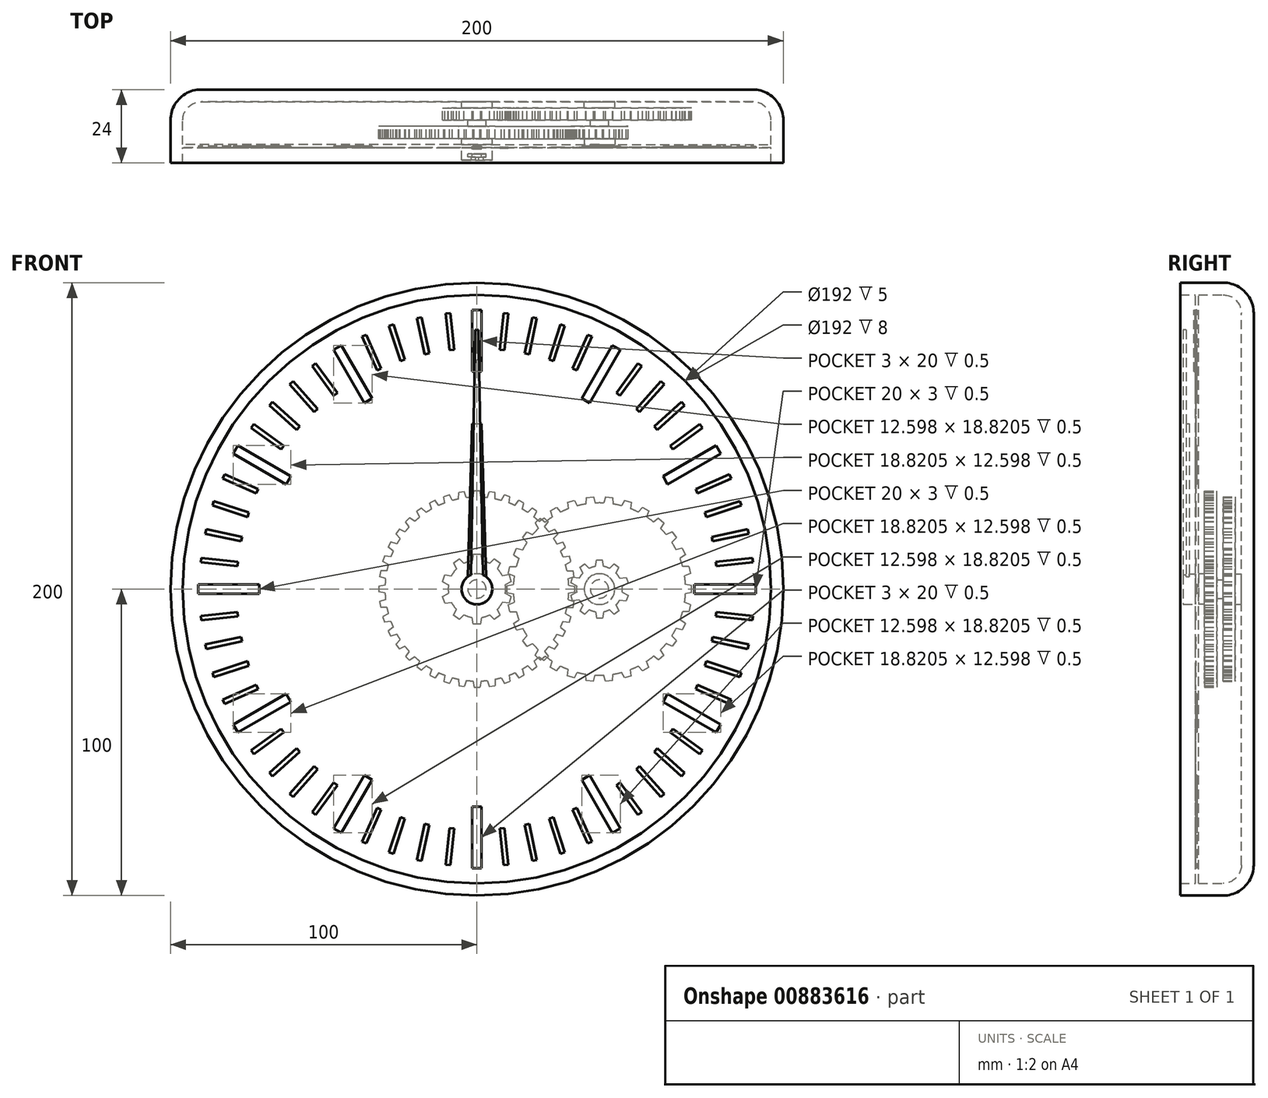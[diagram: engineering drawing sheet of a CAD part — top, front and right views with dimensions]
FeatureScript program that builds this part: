
annotation { "Feature Type Name" : "Feature", "Feature Type Description" : "" }
export const myFeature = defineFeature(function(context is Context, id is Id, definition is map)
    precondition{}
    {
        {
            var Q0;
            Q0=qCreatedBy(makeId("Front.planeOp"),FACE);
            var sketch = newSketch(context, id + "F0", { "sketchPlane" : qUnion([Q0])});
            skCircle(sketch, "E0", {"center": v(0, 0) * mm, "radius": 100 * mm});
            skSolve(sketch);
        }
        {
            var Q0;
            Q0 = qSketchRegion(id + "F0", true);
            extrude(context, id + "F1", {"entities" : qUnion([Q0]), "depth" : 24 * mm, "offsetDistance" : 25 * mm});
        }
        {
            var Q0;
            Q0=makeQuery(id+"F1.opExtrude","CAP_EDGE",EDGE,{"disambiguationData":[OSD([sQuery(id+"F0.wireOp",EDGE,"E0")])],"isStart":true});
            fillet(context, id + "F2", {"entities" : qUnion([Q0]), "radius" : 10 * mm, "tangentPropagation" : true, "allowEdgeOverflow" : false});
        }
        {
            var Q0;
            Q0=makeQuery(id+"F1.opExtrude","CAP_FACE",FACE,{"disambiguationData":[OSD([sQuery(id+"F0.wireOp",EDGE,"E0")])],"isStart":false});
            shell(context, id + "F3", {"entities" : qUnion([Q0]), "thickness" : 4 * mm});
        }
        {
            var Q0;
            {var subQ0=sQuery(id+"F0.wireOp",EDGE,"E0");Q0=makeQuery(id+"F3.opShell","OFFSET_FACE",FACE,{"disambiguationData":[OSD([subQ0]),TDD([makeQuery(id+"F1.opExtrude","CAP_FACE",FACE,{"disambiguationData":[OSD([subQ0])],"isStart":true})])]});}
            var sketch = newSketch(context, id + "F4", { "sketchPlane" : qUnion([Q0])});
            skCircle(sketch, "E1", {"center": v(0, 0) * mm, "radius": 3 * mm});
            skCircle(sketch, "E2", {"center": v(0, 0) * mm, "radius": 5 * mm});
            skCircle(sketch, "E3", {"center": v(40, 0) * mm, "radius": 3 * mm});
            skCircle(sketch, "E4", {"center": v(40, 0) * mm, "radius": 5 * mm});
            skSolve(sketch);
        }
        {
            var Q0;
            Q0 = qSketchRegion(id + "F4", true);
            extrude(context, id + "F5", {"entities" : qUnion([Q0]), "operationType" : NewBodyOperationType.ADD, "depth" : 2 * mm, "offsetDistance" : 25 * mm});
        }
        {
            var Q0;
            {var subQ0=sQuery(id+"F0.wireOp",EDGE,"E0");Q0=makeQuery(id+"F5.boolean.opBoolean","SPLIT",FACE,{"disambiguationData":[TD([makeQuery(id+"F5.opExtrude","SWEPT_FACE",FACE,{"disambiguationData":[OSD([sQuery(id+"F4.wireOp",EDGE,"E1")])]})])],"derivedFrom":makeQuery(id+"F3.opShell","OFFSET_FACE",FACE,{"disambiguationData":[OSD([subQ0]),TDD([makeQuery(id+"F1.opExtrude","CAP_FACE",FACE,{"disambiguationData":[OSD([subQ0])],"isStart":true})])]})});}
            extrude(context, id + "F6", {"entities" : qUnion([Q0]), "depth" : 19 * mm, "offsetDistance" : 25 * mm});
        }
        {
            var Q0;
            {var subQ0=sQuery(id+"F0.wireOp",EDGE,"E0");Q0=makeQuery(id+"F5.boolean.opBoolean","SPLIT",FACE,{"disambiguationData":[TD([makeQuery(id+"F5.opExtrude","SWEPT_FACE",FACE,{"disambiguationData":[OSD([sQuery(id+"F4.wireOp",EDGE,"E3")])]})])],"derivedFrom":makeQuery(id+"F3.opShell","OFFSET_FACE",FACE,{"disambiguationData":[OSD([subQ0]),TDD([makeQuery(id+"F1.opExtrude","CAP_FACE",FACE,{"disambiguationData":[OSD([subQ0])],"isStart":true})])]})});}
            extrude(context, id + "F7", {"entities" : qUnion([Q0]), "depth" : 8 * mm, "offsetDistance" : 25 * mm});
        }
        {
            var Q0;
            Q0=makeQuery(id+"F5.opExtrude","CAP_FACE",FACE,{"disambiguationData":[OSD([sQuery(id+"F4.wireOp",EDGE,"E1"),sQuery(id+"F4.wireOp",EDGE,"E2")])],"isStart":false});
            var sketch = newSketch(context, id + "F8", { "sketchPlane" : qUnion([Q0])});
            skCircle(sketch, "E5", {"center": v(0, 0) * mm, "radius": 9.38 * mm});
            skLineSegment(sketch, "E6", {"start": v(0, 11.38) * mm, "end": v(1.18, 11.38) * mm});
            skLineSegment(sketch, "E7", {"start": v(1.18, 11.38) * mm, "end": v(1.55, 9.25) * mm});
            skLineSegment(sketch, "E8.MirrorCS", {"start": v(0, 11.38) * mm, "end": v(-1.18, 11.38) * mm});
            skLineSegment(sketch, "E9.MirrorCS", {"start": v(-1.18, 11.38) * mm, "end": v(-1.55, 9.25) * mm});
            skLineSegment(sketch, "E10.1.0", {"start": v(-6.69, 9.2) * mm, "end": v(-7.64, 8.51) * mm});
            skLineSegment(sketch, "E10.1.1", {"start": v(-6.69, 9.2) * mm, "end": v(-5.73, 9.9) * mm});
            skLineSegment(sketch, "E10.1.2", {"start": v(-5.73, 9.9) * mm, "end": v(-4.18, 8.4) * mm});
            skLineSegment(sketch, "E10.1.3", {"start": v(-7.64, 8.51) * mm, "end": v(-6.7, 6.57) * mm});
            skLineSegment(sketch, "E10.2.0", {"start": v(-10.82, 3.52) * mm, "end": v(-11.18, 2.4) * mm});
            skLineSegment(sketch, "E10.2.1", {"start": v(-10.82, 3.52) * mm, "end": v(-10.45, 4.64) * mm});
            skLineSegment(sketch, "E10.2.2", {"start": v(-10.45, 4.64) * mm, "end": v(-8.31, 4.33) * mm});
            skLineSegment(sketch, "E10.2.3", {"start": v(-11.18, 2.4) * mm, "end": v(-9.27, 1.38) * mm});
            skLineSegment(sketch, "E11.2.3.0", {"start": v(-10.82, -3.52) * mm, "end": v(-10.45, -4.64) * mm});
            skLineSegment(sketch, "E11.3.3.0", {"start": v(-10.82, -3.52) * mm, "end": v(-11.18, -2.4) * mm});
            skLineSegment(sketch, "E11.6.3.0", {"start": v(-11.18, -2.4) * mm, "end": v(-9.27, -1.38) * mm});
            skLineSegment(sketch, "E11.9.3.0", {"start": v(-10.45, -4.64) * mm, "end": v(-8.31, -4.33) * mm});
            skLineSegment(sketch, "E11.2.4.0", {"start": v(-6.69, -9.2) * mm, "end": v(-5.73, -9.9) * mm});
            skLineSegment(sketch, "E11.3.4.0", {"start": v(-6.69, -9.2) * mm, "end": v(-7.64, -8.51) * mm});
            skLineSegment(sketch, "E11.6.4.0", {"start": v(-7.64, -8.51) * mm, "end": v(-6.7, -6.57) * mm});
            skLineSegment(sketch, "E11.9.4.0", {"start": v(-5.73, -9.9) * mm, "end": v(-4.18, -8.4) * mm});
            skLineSegment(sketch, "E11.2.5.0", {"start": v(0, -11.38) * mm, "end": v(1.18, -11.38) * mm});
            skLineSegment(sketch, "E11.3.5.0", {"start": v(0, -11.38) * mm, "end": v(-1.18, -11.38) * mm});
            skLineSegment(sketch, "E11.6.5.0", {"start": v(-1.18, -11.38) * mm, "end": v(-1.55, -9.25) * mm});
            skLineSegment(sketch, "E11.9.5.0", {"start": v(1.18, -11.38) * mm, "end": v(1.55, -9.25) * mm});
            skLineSegment(sketch, "E11.2.6.0", {"start": v(6.69, -9.2) * mm, "end": v(7.64, -8.51) * mm});
            skLineSegment(sketch, "E11.3.6.0", {"start": v(6.69, -9.2) * mm, "end": v(5.73, -9.9) * mm});
            skLineSegment(sketch, "E11.6.6.0", {"start": v(5.73, -9.9) * mm, "end": v(4.18, -8.4) * mm});
            skLineSegment(sketch, "E11.9.6.0", {"start": v(7.64, -8.51) * mm, "end": v(6.7, -6.57) * mm});
            skLineSegment(sketch, "E11.2.7.0", {"start": v(10.82, -3.52) * mm, "end": v(11.18, -2.4) * mm});
            skLineSegment(sketch, "E11.3.7.0", {"start": v(10.82, -3.52) * mm, "end": v(10.45, -4.64) * mm});
            skLineSegment(sketch, "E11.6.7.0", {"start": v(10.45, -4.64) * mm, "end": v(8.31, -4.33) * mm});
            skLineSegment(sketch, "E11.9.7.0", {"start": v(11.18, -2.4) * mm, "end": v(9.27, -1.38) * mm});
            skLineSegment(sketch, "E11.2.8.0", {"start": v(10.82, 3.52) * mm, "end": v(10.45, 4.64) * mm});
            skLineSegment(sketch, "E11.3.8.0", {"start": v(10.82, 3.52) * mm, "end": v(11.18, 2.4) * mm});
            skLineSegment(sketch, "E11.6.8.0", {"start": v(11.18, 2.4) * mm, "end": v(9.27, 1.38) * mm});
            skLineSegment(sketch, "E11.9.8.0", {"start": v(10.45, 4.64) * mm, "end": v(8.31, 4.33) * mm});
            skLineSegment(sketch, "E11.2.9.0", {"start": v(6.69, 9.2) * mm, "end": v(5.73, 9.9) * mm});
            skLineSegment(sketch, "E11.3.9.0", {"start": v(6.69, 9.2) * mm, "end": v(7.64, 8.51) * mm});
            skLineSegment(sketch, "E11.6.9.0", {"start": v(7.64, 8.51) * mm, "end": v(6.7, 6.57) * mm});
            skLineSegment(sketch, "E11.9.9.0", {"start": v(5.73, 9.9) * mm, "end": v(4.18, 8.4) * mm});
            skSolve(sketch);
        }
        {
            var Q0;
            Q0 = qSketchRegion(id + "F8", true);
            extrude(context, id + "F9", {"entities" : qUnion([Q0]), "operationType" : NewBodyOperationType.ADD, "depth" : 4 * mm, "offsetDistance" : 25 * mm});
        }
        {
            var Q0;
            Q0=makeQuery(id+"F5.opExtrude","CAP_FACE",FACE,{"disambiguationData":[OSD([sQuery(id+"F4.wireOp",EDGE,"E3"),sQuery(id+"F4.wireOp",EDGE,"E4")])],"isStart":false});
            var sketch = newSketch(context, id + "F10", { "sketchPlane" : qUnion([Q0])});
            skCircle(sketch, "E12", {"center": v(40, 0) * mm, "radius": 28.12 * mm});
            skLineSegment(sketch, "E13", {"start": v(9.88, 0) * mm, "end": v(9.88, 1.18) * mm});
            skLineSegment(sketch, "E14", {"start": v(9.88, 1.18) * mm, "end": v(11.92, 1.54) * mm});
            skLineSegment(sketch, "E15.MirrorCS", {"start": v(9.88, 0) * mm, "end": v(9.88, -1.18) * mm});
            skLineSegment(sketch, "E16.MirrorCS", {"start": v(9.88, -1.18) * mm, "end": v(11.92, -1.54) * mm});
            skLineSegment(sketch, "E17.1.0", {"start": v(10.29, -5.11) * mm, "end": v(12.21, -4.33) * mm});
            skLineSegment(sketch, "E17.1.1", {"start": v(10.53, -6.26) * mm, "end": v(10.29, -5.11) * mm});
            skLineSegment(sketch, "E17.1.2", {"start": v(10.53, -6.26) * mm, "end": v(10.78, -7.42) * mm});
            skLineSegment(sketch, "E17.1.3", {"start": v(10.78, -7.42) * mm, "end": v(12.85, -7.34) * mm});
            skLineSegment(sketch, "E17.2.0", {"start": v(12, -11.18) * mm, "end": v(13.72, -10.02) * mm});
            skLineSegment(sketch, "E17.2.1", {"start": v(12.48, -12.25) * mm, "end": v(12, -11.18) * mm});
            skLineSegment(sketch, "E17.2.2", {"start": v(12.48, -12.25) * mm, "end": v(12.96, -13.33) * mm});
            skLineSegment(sketch, "E17.2.3", {"start": v(12.96, -13.33) * mm, "end": v(14.97, -12.83) * mm});
            skLineSegment(sketch, "E18.1.3.0", {"start": v(14.94, -16.75) * mm, "end": v(16.38, -15.26) * mm});
            skLineSegment(sketch, "E18.3.3.0", {"start": v(15.63, -17.7) * mm, "end": v(14.94, -16.75) * mm});
            skLineSegment(sketch, "E18.6.3.0", {"start": v(15.63, -17.7) * mm, "end": v(16.32, -18.66) * mm});
            skLineSegment(sketch, "E18.9.3.0", {"start": v(16.32, -18.66) * mm, "end": v(18.18, -17.75) * mm});
            skLineSegment(sketch, "E18.1.4.0", {"start": v(18.97, -21.6) * mm, "end": v(20.07, -19.84) * mm});
            skLineSegment(sketch, "E18.3.4.0", {"start": v(19.84, -22.39) * mm, "end": v(18.97, -21.6) * mm});
            skLineSegment(sketch, "E18.6.4.0", {"start": v(19.84, -22.39) * mm, "end": v(20.72, -23.18) * mm});
            skLineSegment(sketch, "E18.9.4.0", {"start": v(20.72, -23.18) * mm, "end": v(22.35, -21.9) * mm});
            skLineSegment(sketch, "E18.1.5.0", {"start": v(23.92, -25.5) * mm, "end": v(24.63, -23.55) * mm});
            skLineSegment(sketch, "E18.3.5.0", {"start": v(24.94, -26.09) * mm, "end": v(23.92, -25.5) * mm});
            skLineSegment(sketch, "E18.6.5.0", {"start": v(24.94, -26.09) * mm, "end": v(25.96, -26.68) * mm});
            skLineSegment(sketch, "E18.9.5.0", {"start": v(25.96, -26.68) * mm, "end": v(27.3, -25.09) * mm});
            skLineSegment(sketch, "E18.1.6.0", {"start": v(29.57, -28.29) * mm, "end": v(29.86, -26.23) * mm});
            skLineSegment(sketch, "E18.3.6.0", {"start": v(30.7, -28.65) * mm, "end": v(29.57, -28.29) * mm});
            skLineSegment(sketch, "E18.6.6.0", {"start": v(30.7, -28.65) * mm, "end": v(31.81, -29.01) * mm});
            skLineSegment(sketch, "E18.9.6.0", {"start": v(31.81, -29.01) * mm, "end": v(32.78, -27.18) * mm});
            skLineSegment(sketch, "E18.1.7.0", {"start": v(35.68, -29.84) * mm, "end": v(35.53, -27.77) * mm});
            skLineSegment(sketch, "E18.3.7.0", {"start": v(36.85, -29.96) * mm, "end": v(35.68, -29.84) * mm});
            skLineSegment(sketch, "E18.6.7.0", {"start": v(36.85, -29.96) * mm, "end": v(38.02, -30.08) * mm});
            skLineSegment(sketch, "E18.9.7.0", {"start": v(38.02, -30.08) * mm, "end": v(38.6, -28.09) * mm});
            skLineSegment(sketch, "E18.1.8.0", {"start": v(41.98, -30.08) * mm, "end": v(41.4, -28.09) * mm});
            skLineSegment(sketch, "E18.3.8.0", {"start": v(43.15, -29.96) * mm, "end": v(41.98, -30.08) * mm});
            skLineSegment(sketch, "E18.6.8.0", {"start": v(43.15, -29.96) * mm, "end": v(44.32, -29.84) * mm});
            skLineSegment(sketch, "E18.9.8.0", {"start": v(44.32, -29.84) * mm, "end": v(44.47, -27.77) * mm});
            skLineSegment(sketch, "E18.1.9.0", {"start": v(48.19, -29.01) * mm, "end": v(47.22, -27.18) * mm});
            skLineSegment(sketch, "E18.3.9.0", {"start": v(49.3, -28.65) * mm, "end": v(48.19, -29.01) * mm});
            skLineSegment(sketch, "E18.6.9.0", {"start": v(49.3, -28.65) * mm, "end": v(50.43, -28.29) * mm});
            skLineSegment(sketch, "E18.9.9.0", {"start": v(50.43, -28.29) * mm, "end": v(50.14, -26.23) * mm});
            skLineSegment(sketch, "E18.1.10.0", {"start": v(54.04, -26.68) * mm, "end": v(52.7, -25.09) * mm});
            skLineSegment(sketch, "E18.3.10.0", {"start": v(55.06, -26.09) * mm, "end": v(54.04, -26.68) * mm});
            skLineSegment(sketch, "E18.6.10.0", {"start": v(55.06, -26.09) * mm, "end": v(56.08, -25.5) * mm});
            skLineSegment(sketch, "E18.9.10.0", {"start": v(56.08, -25.5) * mm, "end": v(55.37, -23.55) * mm});
            skLineSegment(sketch, "E18.1.11.0", {"start": v(59.28, -23.18) * mm, "end": v(57.65, -21.9) * mm});
            skLineSegment(sketch, "E18.3.11.0", {"start": v(60.16, -22.39) * mm, "end": v(59.28, -23.18) * mm});
            skLineSegment(sketch, "E18.6.11.0", {"start": v(60.16, -22.39) * mm, "end": v(61.03, -21.6) * mm});
            skLineSegment(sketch, "E18.9.11.0", {"start": v(61.03, -21.6) * mm, "end": v(59.93, -19.84) * mm});
            skLineSegment(sketch, "E18.1.12.0", {"start": v(63.68, -18.66) * mm, "end": v(61.82, -17.75) * mm});
            skLineSegment(sketch, "E18.3.12.0", {"start": v(64.37, -17.7) * mm, "end": v(63.68, -18.66) * mm});
            skLineSegment(sketch, "E18.6.12.0", {"start": v(64.37, -17.7) * mm, "end": v(65.06, -16.75) * mm});
            skLineSegment(sketch, "E18.9.12.0", {"start": v(65.06, -16.75) * mm, "end": v(63.62, -15.26) * mm});
            skLineSegment(sketch, "E18.1.13.0", {"start": v(67.04, -13.33) * mm, "end": v(65.03, -12.83) * mm});
            skLineSegment(sketch, "E18.3.13.0", {"start": v(67.52, -12.25) * mm, "end": v(67.04, -13.33) * mm});
            skLineSegment(sketch, "E18.6.13.0", {"start": v(67.52, -12.25) * mm, "end": v(68, -11.18) * mm});
            skLineSegment(sketch, "E18.9.13.0", {"start": v(68, -11.18) * mm, "end": v(66.28, -10.02) * mm});
            skLineSegment(sketch, "E18.1.14.0", {"start": v(69.22, -7.42) * mm, "end": v(67.15, -7.34) * mm});
            skLineSegment(sketch, "E18.3.14.0", {"start": v(69.47, -6.26) * mm, "end": v(69.22, -7.42) * mm});
            skLineSegment(sketch, "E18.6.14.0", {"start": v(69.47, -6.26) * mm, "end": v(69.71, -5.11) * mm});
            skLineSegment(sketch, "E18.9.14.0", {"start": v(69.71, -5.11) * mm, "end": v(67.79, -4.33) * mm});
            skLineSegment(sketch, "E18.1.15.0", {"start": v(70.13, -1.18) * mm, "end": v(68.08, -1.54) * mm});
            skLineSegment(sketch, "E18.3.15.0", {"start": v(70.12, 0) * mm, "end": v(70.12, -1.18) * mm});
            skLineSegment(sketch, "E18.6.15.0", {"start": v(70.12, 0) * mm, "end": v(70.12, 1.18) * mm});
            skLineSegment(sketch, "E18.9.15.0", {"start": v(70.13, 1.18) * mm, "end": v(68.08, 1.54) * mm});
            skLineSegment(sketch, "E18.1.16.0", {"start": v(69.71, 5.11) * mm, "end": v(67.79, 4.33) * mm});
            skLineSegment(sketch, "E18.3.16.0", {"start": v(69.47, 6.26) * mm, "end": v(69.71, 5.11) * mm});
            skLineSegment(sketch, "E18.6.16.0", {"start": v(69.47, 6.26) * mm, "end": v(69.22, 7.42) * mm});
            skLineSegment(sketch, "E18.9.16.0", {"start": v(69.22, 7.42) * mm, "end": v(67.15, 7.34) * mm});
            skLineSegment(sketch, "E18.1.17.0", {"start": v(68, 11.18) * mm, "end": v(66.28, 10.02) * mm});
            skLineSegment(sketch, "E18.3.17.0", {"start": v(67.52, 12.25) * mm, "end": v(68, 11.18) * mm});
            skLineSegment(sketch, "E18.6.17.0", {"start": v(67.52, 12.25) * mm, "end": v(67.04, 13.33) * mm});
            skLineSegment(sketch, "E18.9.17.0", {"start": v(67.04, 13.33) * mm, "end": v(65.03, 12.83) * mm});
            skLineSegment(sketch, "E18.1.18.0", {"start": v(65.06, 16.75) * mm, "end": v(63.62, 15.26) * mm});
            skLineSegment(sketch, "E18.3.18.0", {"start": v(64.37, 17.7) * mm, "end": v(65.06, 16.75) * mm});
            skLineSegment(sketch, "E18.6.18.0", {"start": v(64.37, 17.7) * mm, "end": v(63.68, 18.66) * mm});
            skLineSegment(sketch, "E18.9.18.0", {"start": v(63.68, 18.66) * mm, "end": v(61.82, 17.75) * mm});
            skLineSegment(sketch, "E18.1.19.0", {"start": v(61.03, 21.6) * mm, "end": v(59.93, 19.84) * mm});
            skLineSegment(sketch, "E18.3.19.0", {"start": v(60.16, 22.39) * mm, "end": v(61.03, 21.6) * mm});
            skLineSegment(sketch, "E18.6.19.0", {"start": v(60.16, 22.39) * mm, "end": v(59.28, 23.18) * mm});
            skLineSegment(sketch, "E18.9.19.0", {"start": v(59.28, 23.18) * mm, "end": v(57.65, 21.9) * mm});
            skLineSegment(sketch, "E18.1.20.0", {"start": v(56.08, 25.5) * mm, "end": v(55.37, 23.55) * mm});
            skLineSegment(sketch, "E18.3.20.0", {"start": v(55.06, 26.09) * mm, "end": v(56.08, 25.5) * mm});
            skLineSegment(sketch, "E18.6.20.0", {"start": v(55.06, 26.09) * mm, "end": v(54.04, 26.68) * mm});
            skLineSegment(sketch, "E18.9.20.0", {"start": v(54.04, 26.68) * mm, "end": v(52.7, 25.09) * mm});
            skLineSegment(sketch, "E18.1.21.0", {"start": v(50.43, 28.29) * mm, "end": v(50.14, 26.23) * mm});
            skLineSegment(sketch, "E18.3.21.0", {"start": v(49.3, 28.65) * mm, "end": v(50.43, 28.29) * mm});
            skLineSegment(sketch, "E18.6.21.0", {"start": v(49.3, 28.65) * mm, "end": v(48.19, 29.01) * mm});
            skLineSegment(sketch, "E18.9.21.0", {"start": v(48.19, 29.01) * mm, "end": v(47.22, 27.18) * mm});
            skLineSegment(sketch, "E18.1.22.0", {"start": v(44.32, 29.84) * mm, "end": v(44.47, 27.77) * mm});
            skLineSegment(sketch, "E18.3.22.0", {"start": v(43.15, 29.96) * mm, "end": v(44.32, 29.84) * mm});
            skLineSegment(sketch, "E18.6.22.0", {"start": v(43.15, 29.96) * mm, "end": v(41.98, 30.08) * mm});
            skLineSegment(sketch, "E18.9.22.0", {"start": v(41.98, 30.08) * mm, "end": v(41.4, 28.09) * mm});
            skLineSegment(sketch, "E18.1.23.0", {"start": v(38.02, 30.08) * mm, "end": v(38.6, 28.09) * mm});
            skLineSegment(sketch, "E18.3.23.0", {"start": v(36.85, 29.96) * mm, "end": v(38.02, 30.08) * mm});
            skLineSegment(sketch, "E18.6.23.0", {"start": v(36.85, 29.96) * mm, "end": v(35.68, 29.84) * mm});
            skLineSegment(sketch, "E18.9.23.0", {"start": v(35.68, 29.84) * mm, "end": v(35.53, 27.77) * mm});
            skLineSegment(sketch, "E18.1.24.0", {"start": v(31.81, 29.01) * mm, "end": v(32.78, 27.18) * mm});
            skLineSegment(sketch, "E18.3.24.0", {"start": v(30.7, 28.65) * mm, "end": v(31.81, 29.01) * mm});
            skLineSegment(sketch, "E18.6.24.0", {"start": v(30.7, 28.65) * mm, "end": v(29.57, 28.29) * mm});
            skLineSegment(sketch, "E18.9.24.0", {"start": v(29.57, 28.29) * mm, "end": v(29.86, 26.23) * mm});
            skLineSegment(sketch, "E18.1.25.0", {"start": v(25.96, 26.68) * mm, "end": v(27.3, 25.09) * mm});
            skLineSegment(sketch, "E18.3.25.0", {"start": v(24.94, 26.09) * mm, "end": v(25.96, 26.68) * mm});
            skLineSegment(sketch, "E18.6.25.0", {"start": v(24.94, 26.09) * mm, "end": v(23.92, 25.5) * mm});
            skLineSegment(sketch, "E18.9.25.0", {"start": v(23.92, 25.5) * mm, "end": v(24.63, 23.55) * mm});
            skLineSegment(sketch, "E18.1.26.0", {"start": v(20.72, 23.18) * mm, "end": v(22.35, 21.9) * mm});
            skLineSegment(sketch, "E18.3.26.0", {"start": v(19.84, 22.39) * mm, "end": v(20.72, 23.18) * mm});
            skLineSegment(sketch, "E18.6.26.0", {"start": v(19.84, 22.39) * mm, "end": v(18.97, 21.6) * mm});
            skLineSegment(sketch, "E18.9.26.0", {"start": v(18.97, 21.6) * mm, "end": v(20.07, 19.84) * mm});
            skLineSegment(sketch, "E18.1.27.0", {"start": v(16.32, 18.66) * mm, "end": v(18.18, 17.75) * mm});
            skLineSegment(sketch, "E18.3.27.0", {"start": v(15.63, 17.7) * mm, "end": v(16.32, 18.66) * mm});
            skLineSegment(sketch, "E18.6.27.0", {"start": v(15.63, 17.7) * mm, "end": v(14.94, 16.75) * mm});
            skLineSegment(sketch, "E18.9.27.0", {"start": v(14.94, 16.75) * mm, "end": v(16.38, 15.26) * mm});
            skLineSegment(sketch, "E18.1.28.0", {"start": v(12.96, 13.33) * mm, "end": v(14.97, 12.83) * mm});
            skLineSegment(sketch, "E18.3.28.0", {"start": v(12.48, 12.25) * mm, "end": v(12.96, 13.33) * mm});
            skLineSegment(sketch, "E18.6.28.0", {"start": v(12.48, 12.25) * mm, "end": v(12, 11.18) * mm});
            skLineSegment(sketch, "E18.9.28.0", {"start": v(12, 11.18) * mm, "end": v(13.72, 10.02) * mm});
            skLineSegment(sketch, "E18.1.29.0", {"start": v(10.78, 7.42) * mm, "end": v(12.85, 7.34) * mm});
            skLineSegment(sketch, "E18.3.29.0", {"start": v(10.53, 6.26) * mm, "end": v(10.78, 7.42) * mm});
            skLineSegment(sketch, "E18.6.29.0", {"start": v(10.53, 6.26) * mm, "end": v(10.29, 5.11) * mm});
            skLineSegment(sketch, "E18.9.29.0", {"start": v(10.29, 5.11) * mm, "end": v(12.21, 4.33) * mm});
            skSolve(sketch);
        }
        {
            var Q0;
            Q0 = qSketchRegion(id + "F10", true);
            extrude(context, id + "F11", {"entities" : qUnion([Q0]), "operationType" : NewBodyOperationType.ADD, "depth" : 4 * mm, "offsetDistance" : 25 * mm});
        }
        {
            var Q0;
            Q0=makeQuery(id+"F9.opExtrude","CAP_FACE",FACE,{"disambiguationData":[OSD([sQuery(id+"F8.wireOp",EDGE,"E5"),sQuery(id+"F8.wireOp",EDGE,"E6"),sQuery(id+"F8.wireOp",EDGE,"E7"),sQuery(id+"F8.wireOp",EDGE,"E8.MirrorCS"),sQuery(id+"F8.wireOp",EDGE,"E9.MirrorCS"),sQuery(id+"F8.wireOp",EDGE,"E10.1.0"),sQuery(id+"F8.wireOp",EDGE,"E10.1.1"),sQuery(id+"F8.wireOp",EDGE,"E10.1.2"),sQuery(id+"F8.wireOp",EDGE,"E10.1.3"),sQuery(id+"F8.wireOp",EDGE,"E10.2.0"),sQuery(id+"F8.wireOp",EDGE,"E10.2.1"),sQuery(id+"F8.wireOp",EDGE,"E10.2.2"),sQuery(id+"F8.wireOp",EDGE,"E10.2.3"),sQuery(id+"F8.wireOp",EDGE,"E11.2.3.0"),sQuery(id+"F8.wireOp",EDGE,"E11.3.3.0"),sQuery(id+"F8.wireOp",EDGE,"E11.6.3.0"),sQuery(id+"F8.wireOp",EDGE,"E11.9.3.0"),sQuery(id+"F8.wireOp",EDGE,"E11.2.4.0"),sQuery(id+"F8.wireOp",EDGE,"E11.3.4.0"),sQuery(id+"F8.wireOp",EDGE,"E11.6.4.0"),sQuery(id+"F8.wireOp",EDGE,"E11.9.4.0"),sQuery(id+"F8.wireOp",EDGE,"E11.2.5.0"),sQuery(id+"F8.wireOp",EDGE,"E11.3.5.0"),sQuery(id+"F8.wireOp",EDGE,"E11.6.5.0"),sQuery(id+"F8.wireOp",EDGE,"E11.9.5.0"),sQuery(id+"F8.wireOp",EDGE,"E11.2.6.0"),sQuery(id+"F8.wireOp",EDGE,"E11.3.6.0"),sQuery(id+"F8.wireOp",EDGE,"E11.6.6.0"),sQuery(id+"F8.wireOp",EDGE,"E11.9.6.0"),sQuery(id+"F8.wireOp",EDGE,"E11.2.7.0"),sQuery(id+"F8.wireOp",EDGE,"E11.3.7.0"),sQuery(id+"F8.wireOp",EDGE,"E11.6.7.0"),sQuery(id+"F8.wireOp",EDGE,"E11.9.7.0"),sQuery(id+"F8.wireOp",EDGE,"E11.2.8.0"),sQuery(id+"F8.wireOp",EDGE,"E11.3.8.0"),sQuery(id+"F8.wireOp",EDGE,"E11.6.8.0"),sQuery(id+"F8.wireOp",EDGE,"E11.9.8.0"),sQuery(id+"F8.wireOp",EDGE,"E11.2.9.0"),sQuery(id+"F8.wireOp",EDGE,"E11.3.9.0"),sQuery(id+"F8.wireOp",EDGE,"E11.6.9.0"),sQuery(id+"F8.wireOp",EDGE,"E11.9.9.0")])],"isStart":false});
            var sketch = newSketch(context, id + "F12", { "sketchPlane" : qUnion([Q0])});
            skCircle(sketch, "E19.0", {"center": v(0, 0) * mm, "radius": 3 * mm});
            skCircle(sketch, "E20.0", {"center": v(0, 0) * mm, "radius": 5 * mm});
            skSolve(sketch);
        }
        {
            var Q0;
            Q0=makeQuery(id+"F12.imprint","IMPRINT",FACE,{"disambiguationData":[TD([[makeQuery(id+"F12.imprint","IMPRINT",EDGE,{"derivedFrom":sQuery(id+"F12.wireOp",EDGE,"E19.0")}),-1.0]])]});
            extrude(context, id + "F13", {"entities" : qUnion([Q0]), "depth" : 2 * mm, "offsetDistance" : 25 * mm});
        }
        {
            var Q0;
            Q0=makeQuery(id+"F13.opExtrude","CAP_FACE",FACE,{"disambiguationData":[OSD([sQuery(id+"F12.wireOp",EDGE,"E19.0"),sQuery(id+"F12.wireOp",EDGE,"E20.0")])],"isStart":false});
            var sketch = newSketch(context, id + "F14", { "sketchPlane" : qUnion([Q0])});
            skCircle(sketch, "E21.0", {"center": v(0, 0) * mm, "radius": 3 * mm});
            skCircle(sketch, "E22", {"center": v(0, 0) * mm, "radius": 30 * mm});
            skLineSegment(sketch, "E23", {"start": v(-1.3, 29.97) * mm, "end": v(-0.94, 32) * mm});
            skLineSegment(sketch, "E24", {"start": v(-0.94, 32) * mm, "end": v(0, 32) * mm});
            skLineSegment(sketch, "E25.MirrorCS", {"start": v(1.3, 29.97) * mm, "end": v(0.94, 32) * mm});
            skLineSegment(sketch, "E26.MirrorCS", {"start": v(0.94, 32) * mm, "end": v(0, 32) * mm});
            skLineSegment(sketch, "E27.1.0", {"start": v(-3.4, 29.8) * mm, "end": v(-4.08, 31.75) * mm});
            skLineSegment(sketch, "E27.1.1", {"start": v(-4.08, 31.75) * mm, "end": v(-5, 31.6) * mm});
            skLineSegment(sketch, "E27.1.2", {"start": v(-5.94, 31.46) * mm, "end": v(-5, 31.6) * mm});
            skLineSegment(sketch, "E27.1.3", {"start": v(-5.97, 29.4) * mm, "end": v(-5.94, 31.46) * mm});
            skLineSegment(sketch, "E27.2.0", {"start": v(-8.03, 28.9) * mm, "end": v(-9, 30.73) * mm});
            skLineSegment(sketch, "E27.2.1", {"start": v(-9, 30.73) * mm, "end": v(-9.89, 30.43) * mm});
            skLineSegment(sketch, "E27.2.2", {"start": v(-10.78, 30.14) * mm, "end": v(-9.89, 30.43) * mm});
            skLineSegment(sketch, "E27.2.3", {"start": v(-10.5, 28.1) * mm, "end": v(-10.78, 30.14) * mm});
            skLineSegment(sketch, "E28.1.3.0", {"start": v(-12.45, 27.3) * mm, "end": v(-13.69, 28.94) * mm});
            skLineSegment(sketch, "E28.3.3.0", {"start": v(-13.69, 28.94) * mm, "end": v(-14.53, 28.51) * mm});
            skLineSegment(sketch, "E28.6.3.0", {"start": v(-15.37, 28.08) * mm, "end": v(-14.53, 28.51) * mm});
            skLineSegment(sketch, "E28.9.3.0", {"start": v(-14.77, 26.11) * mm, "end": v(-15.37, 28.08) * mm});
            skLineSegment(sketch, "E28.1.4.0", {"start": v(-16.57, 25.01) * mm, "end": v(-18.05, 26.44) * mm});
            skLineSegment(sketch, "E28.3.4.0", {"start": v(-18.05, 26.44) * mm, "end": v(-18.8, 25.89) * mm});
            skLineSegment(sketch, "E28.6.4.0", {"start": v(-19.57, 25.33) * mm, "end": v(-18.8, 25.89) * mm});
            skLineSegment(sketch, "E28.9.4.0", {"start": v(-18.67, 23.48) * mm, "end": v(-19.57, 25.33) * mm});
            skLineSegment(sketch, "E28.1.5.0", {"start": v(-20.27, 22.11) * mm, "end": v(-21.96, 23.3) * mm});
            skLineSegment(sketch, "E28.3.5.0", {"start": v(-21.96, 23.3) * mm, "end": v(-22.63, 22.63) * mm});
            skLineSegment(sketch, "E28.6.5.0", {"start": v(-23.3, 21.96) * mm, "end": v(-22.63, 22.63) * mm});
            skLineSegment(sketch, "E28.9.5.0", {"start": v(-22.11, 20.27) * mm, "end": v(-23.3, 21.96) * mm});
            skLineSegment(sketch, "E28.1.6.0", {"start": v(-23.48, 18.67) * mm, "end": v(-25.33, 19.57) * mm});
            skLineSegment(sketch, "E28.3.6.0", {"start": v(-25.33, 19.57) * mm, "end": v(-25.89, 18.8) * mm});
            skLineSegment(sketch, "E28.6.6.0", {"start": v(-26.44, 18.05) * mm, "end": v(-25.89, 18.8) * mm});
            skLineSegment(sketch, "E28.9.6.0", {"start": v(-25.01, 16.57) * mm, "end": v(-26.44, 18.05) * mm});
            skLineSegment(sketch, "E28.1.7.0", {"start": v(-26.11, 14.77) * mm, "end": v(-28.08, 15.37) * mm});
            skLineSegment(sketch, "E28.3.7.0", {"start": v(-28.08, 15.37) * mm, "end": v(-28.51, 14.53) * mm});
            skLineSegment(sketch, "E28.6.7.0", {"start": v(-28.94, 13.69) * mm, "end": v(-28.51, 14.53) * mm});
            skLineSegment(sketch, "E28.9.7.0", {"start": v(-27.3, 12.45) * mm, "end": v(-28.94, 13.69) * mm});
            skLineSegment(sketch, "E28.1.8.0", {"start": v(-28.1, 10.5) * mm, "end": v(-30.14, 10.78) * mm});
            skLineSegment(sketch, "E28.3.8.0", {"start": v(-30.14, 10.78) * mm, "end": v(-30.43, 9.89) * mm});
            skLineSegment(sketch, "E28.6.8.0", {"start": v(-30.73, 9) * mm, "end": v(-30.43, 9.89) * mm});
            skLineSegment(sketch, "E28.9.8.0", {"start": v(-28.9, 8.03) * mm, "end": v(-30.73, 9) * mm});
            skLineSegment(sketch, "E28.1.9.0", {"start": v(-29.4, 5.97) * mm, "end": v(-31.46, 5.94) * mm});
            skLineSegment(sketch, "E28.3.9.0", {"start": v(-31.46, 5.94) * mm, "end": v(-31.6, 5) * mm});
            skLineSegment(sketch, "E28.6.9.0", {"start": v(-31.75, 4.08) * mm, "end": v(-31.6, 5) * mm});
            skLineSegment(sketch, "E28.9.9.0", {"start": v(-29.8, 3.4) * mm, "end": v(-31.75, 4.08) * mm});
            skLineSegment(sketch, "E28.1.10.0", {"start": v(-29.97, 1.3) * mm, "end": v(-32, 0.94) * mm});
            skLineSegment(sketch, "E28.3.10.0", {"start": v(-32, 0.94) * mm, "end": v(-32, 0) * mm});
            skLineSegment(sketch, "E28.6.10.0", {"start": v(-32, -0.94) * mm, "end": v(-32, 0) * mm});
            skLineSegment(sketch, "E28.9.10.0", {"start": v(-29.97, -1.3) * mm, "end": v(-32, -0.94) * mm});
            skLineSegment(sketch, "E28.1.11.0", {"start": v(-29.8, -3.4) * mm, "end": v(-31.75, -4.08) * mm});
            skLineSegment(sketch, "E28.3.11.0", {"start": v(-31.75, -4.08) * mm, "end": v(-31.6, -5) * mm});
            skLineSegment(sketch, "E28.6.11.0", {"start": v(-31.46, -5.94) * mm, "end": v(-31.6, -5) * mm});
            skLineSegment(sketch, "E28.9.11.0", {"start": v(-29.4, -5.97) * mm, "end": v(-31.46, -5.94) * mm});
            skLineSegment(sketch, "E28.1.12.0", {"start": v(-28.9, -8.03) * mm, "end": v(-30.73, -9) * mm});
            skLineSegment(sketch, "E28.3.12.0", {"start": v(-30.73, -9) * mm, "end": v(-30.43, -9.89) * mm});
            skLineSegment(sketch, "E28.6.12.0", {"start": v(-30.14, -10.78) * mm, "end": v(-30.43, -9.89) * mm});
            skLineSegment(sketch, "E28.9.12.0", {"start": v(-28.1, -10.5) * mm, "end": v(-30.14, -10.78) * mm});
            skLineSegment(sketch, "E28.1.13.0", {"start": v(-27.3, -12.45) * mm, "end": v(-28.94, -13.69) * mm});
            skLineSegment(sketch, "E28.3.13.0", {"start": v(-28.94, -13.69) * mm, "end": v(-28.51, -14.53) * mm});
            skLineSegment(sketch, "E28.6.13.0", {"start": v(-28.08, -15.37) * mm, "end": v(-28.51, -14.53) * mm});
            skLineSegment(sketch, "E28.9.13.0", {"start": v(-26.11, -14.77) * mm, "end": v(-28.08, -15.37) * mm});
            skLineSegment(sketch, "E28.1.14.0", {"start": v(-25.01, -16.57) * mm, "end": v(-26.44, -18.05) * mm});
            skLineSegment(sketch, "E28.3.14.0", {"start": v(-26.44, -18.05) * mm, "end": v(-25.89, -18.8) * mm});
            skLineSegment(sketch, "E28.6.14.0", {"start": v(-25.33, -19.57) * mm, "end": v(-25.89, -18.8) * mm});
            skLineSegment(sketch, "E28.9.14.0", {"start": v(-23.48, -18.67) * mm, "end": v(-25.33, -19.57) * mm});
            skLineSegment(sketch, "E28.1.15.0", {"start": v(-22.11, -20.27) * mm, "end": v(-23.3, -21.96) * mm});
            skLineSegment(sketch, "E28.3.15.0", {"start": v(-23.3, -21.96) * mm, "end": v(-22.63, -22.63) * mm});
            skLineSegment(sketch, "E28.6.15.0", {"start": v(-21.96, -23.3) * mm, "end": v(-22.63, -22.63) * mm});
            skLineSegment(sketch, "E28.9.15.0", {"start": v(-20.27, -22.11) * mm, "end": v(-21.96, -23.3) * mm});
            skLineSegment(sketch, "E28.1.16.0", {"start": v(-18.67, -23.48) * mm, "end": v(-19.57, -25.33) * mm});
            skLineSegment(sketch, "E28.3.16.0", {"start": v(-19.57, -25.33) * mm, "end": v(-18.8, -25.89) * mm});
            skLineSegment(sketch, "E28.6.16.0", {"start": v(-18.05, -26.44) * mm, "end": v(-18.8, -25.89) * mm});
            skLineSegment(sketch, "E28.9.16.0", {"start": v(-16.57, -25.01) * mm, "end": v(-18.05, -26.44) * mm});
            skLineSegment(sketch, "E28.1.17.0", {"start": v(-14.77, -26.11) * mm, "end": v(-15.37, -28.08) * mm});
            skLineSegment(sketch, "E28.3.17.0", {"start": v(-15.37, -28.08) * mm, "end": v(-14.53, -28.51) * mm});
            skLineSegment(sketch, "E28.6.17.0", {"start": v(-13.69, -28.94) * mm, "end": v(-14.53, -28.51) * mm});
            skLineSegment(sketch, "E28.9.17.0", {"start": v(-12.45, -27.3) * mm, "end": v(-13.69, -28.94) * mm});
            skLineSegment(sketch, "E28.1.18.0", {"start": v(-10.5, -28.1) * mm, "end": v(-10.78, -30.14) * mm});
            skLineSegment(sketch, "E28.3.18.0", {"start": v(-10.78, -30.14) * mm, "end": v(-9.89, -30.43) * mm});
            skLineSegment(sketch, "E28.6.18.0", {"start": v(-9, -30.73) * mm, "end": v(-9.89, -30.43) * mm});
            skLineSegment(sketch, "E28.9.18.0", {"start": v(-8.03, -28.9) * mm, "end": v(-9, -30.73) * mm});
            skLineSegment(sketch, "E28.1.19.0", {"start": v(-5.97, -29.4) * mm, "end": v(-5.94, -31.46) * mm});
            skLineSegment(sketch, "E28.3.19.0", {"start": v(-5.94, -31.46) * mm, "end": v(-5, -31.6) * mm});
            skLineSegment(sketch, "E28.6.19.0", {"start": v(-4.08, -31.75) * mm, "end": v(-5, -31.6) * mm});
            skLineSegment(sketch, "E28.9.19.0", {"start": v(-3.4, -29.8) * mm, "end": v(-4.08, -31.75) * mm});
            skLineSegment(sketch, "E28.1.20.0", {"start": v(-1.3, -29.97) * mm, "end": v(-0.94, -32) * mm});
            skLineSegment(sketch, "E28.3.20.0", {"start": v(-0.94, -32) * mm, "end": v(0, -32) * mm});
            skLineSegment(sketch, "E28.6.20.0", {"start": v(0.94, -32) * mm, "end": v(0, -32) * mm});
            skLineSegment(sketch, "E28.9.20.0", {"start": v(1.3, -29.97) * mm, "end": v(0.94, -32) * mm});
            skLineSegment(sketch, "E28.1.21.0", {"start": v(3.4, -29.8) * mm, "end": v(4.08, -31.75) * mm});
            skLineSegment(sketch, "E28.3.21.0", {"start": v(4.08, -31.75) * mm, "end": v(5, -31.6) * mm});
            skLineSegment(sketch, "E28.6.21.0", {"start": v(5.94, -31.46) * mm, "end": v(5, -31.6) * mm});
            skLineSegment(sketch, "E28.9.21.0", {"start": v(5.97, -29.4) * mm, "end": v(5.94, -31.46) * mm});
            skLineSegment(sketch, "E28.1.22.0", {"start": v(8.03, -28.9) * mm, "end": v(9, -30.73) * mm});
            skLineSegment(sketch, "E28.3.22.0", {"start": v(9, -30.73) * mm, "end": v(9.89, -30.43) * mm});
            skLineSegment(sketch, "E28.6.22.0", {"start": v(10.78, -30.14) * mm, "end": v(9.89, -30.43) * mm});
            skLineSegment(sketch, "E28.9.22.0", {"start": v(10.5, -28.1) * mm, "end": v(10.78, -30.14) * mm});
            skLineSegment(sketch, "E28.1.23.0", {"start": v(12.45, -27.3) * mm, "end": v(13.69, -28.94) * mm});
            skLineSegment(sketch, "E28.3.23.0", {"start": v(13.69, -28.94) * mm, "end": v(14.53, -28.51) * mm});
            skLineSegment(sketch, "E28.6.23.0", {"start": v(15.37, -28.08) * mm, "end": v(14.53, -28.51) * mm});
            skLineSegment(sketch, "E28.9.23.0", {"start": v(14.77, -26.11) * mm, "end": v(15.37, -28.08) * mm});
            skLineSegment(sketch, "E28.1.24.0", {"start": v(16.57, -25.01) * mm, "end": v(18.05, -26.44) * mm});
            skLineSegment(sketch, "E28.3.24.0", {"start": v(18.05, -26.44) * mm, "end": v(18.8, -25.89) * mm});
            skLineSegment(sketch, "E28.6.24.0", {"start": v(19.57, -25.33) * mm, "end": v(18.8, -25.89) * mm});
            skLineSegment(sketch, "E28.9.24.0", {"start": v(18.67, -23.48) * mm, "end": v(19.57, -25.33) * mm});
            skLineSegment(sketch, "E28.1.25.0", {"start": v(20.27, -22.11) * mm, "end": v(21.96, -23.3) * mm});
            skLineSegment(sketch, "E28.3.25.0", {"start": v(21.96, -23.3) * mm, "end": v(22.63, -22.63) * mm});
            skLineSegment(sketch, "E28.6.25.0", {"start": v(23.3, -21.96) * mm, "end": v(22.63, -22.63) * mm});
            skLineSegment(sketch, "E28.9.25.0", {"start": v(22.11, -20.27) * mm, "end": v(23.3, -21.96) * mm});
            skLineSegment(sketch, "E28.1.26.0", {"start": v(23.48, -18.67) * mm, "end": v(25.33, -19.57) * mm});
            skLineSegment(sketch, "E28.3.26.0", {"start": v(25.33, -19.57) * mm, "end": v(25.89, -18.8) * mm});
            skLineSegment(sketch, "E28.6.26.0", {"start": v(26.44, -18.05) * mm, "end": v(25.89, -18.8) * mm});
            skLineSegment(sketch, "E28.9.26.0", {"start": v(25.01, -16.57) * mm, "end": v(26.44, -18.05) * mm});
            skLineSegment(sketch, "E28.1.27.0", {"start": v(26.11, -14.77) * mm, "end": v(28.08, -15.37) * mm});
            skLineSegment(sketch, "E28.3.27.0", {"start": v(28.08, -15.37) * mm, "end": v(28.51, -14.53) * mm});
            skLineSegment(sketch, "E28.6.27.0", {"start": v(28.94, -13.69) * mm, "end": v(28.51, -14.53) * mm});
            skLineSegment(sketch, "E28.9.27.0", {"start": v(27.3, -12.45) * mm, "end": v(28.94, -13.69) * mm});
            skLineSegment(sketch, "E28.1.28.0", {"start": v(28.1, -10.5) * mm, "end": v(30.14, -10.78) * mm});
            skLineSegment(sketch, "E28.3.28.0", {"start": v(30.14, -10.78) * mm, "end": v(30.43, -9.89) * mm});
            skLineSegment(sketch, "E28.6.28.0", {"start": v(30.73, -9) * mm, "end": v(30.43, -9.89) * mm});
            skLineSegment(sketch, "E28.9.28.0", {"start": v(28.9, -8.03) * mm, "end": v(30.73, -9) * mm});
            skLineSegment(sketch, "E28.1.29.0", {"start": v(29.4, -5.97) * mm, "end": v(31.46, -5.94) * mm});
            skLineSegment(sketch, "E28.3.29.0", {"start": v(31.46, -5.94) * mm, "end": v(31.6, -5) * mm});
            skLineSegment(sketch, "E28.6.29.0", {"start": v(31.75, -4.08) * mm, "end": v(31.6, -5) * mm});
            skLineSegment(sketch, "E28.9.29.0", {"start": v(29.8, -3.4) * mm, "end": v(31.75, -4.08) * mm});
            skLineSegment(sketch, "E28.1.30.0", {"start": v(29.97, -1.3) * mm, "end": v(32, -0.94) * mm});
            skLineSegment(sketch, "E28.3.30.0", {"start": v(32, -0.94) * mm, "end": v(32, 0) * mm});
            skLineSegment(sketch, "E28.6.30.0", {"start": v(32, 0.94) * mm, "end": v(32, 0) * mm});
            skLineSegment(sketch, "E28.9.30.0", {"start": v(29.97, 1.3) * mm, "end": v(32, 0.94) * mm});
            skLineSegment(sketch, "E28.1.31.0", {"start": v(29.8, 3.4) * mm, "end": v(31.75, 4.08) * mm});
            skLineSegment(sketch, "E28.3.31.0", {"start": v(31.75, 4.08) * mm, "end": v(31.6, 5) * mm});
            skLineSegment(sketch, "E28.6.31.0", {"start": v(31.46, 5.94) * mm, "end": v(31.6, 5) * mm});
            skLineSegment(sketch, "E28.9.31.0", {"start": v(29.4, 5.97) * mm, "end": v(31.46, 5.94) * mm});
            skLineSegment(sketch, "E28.1.32.0", {"start": v(28.9, 8.03) * mm, "end": v(30.73, 9) * mm});
            skLineSegment(sketch, "E28.3.32.0", {"start": v(30.73, 9) * mm, "end": v(30.43, 9.89) * mm});
            skLineSegment(sketch, "E28.6.32.0", {"start": v(30.14, 10.78) * mm, "end": v(30.43, 9.89) * mm});
            skLineSegment(sketch, "E28.9.32.0", {"start": v(28.1, 10.5) * mm, "end": v(30.14, 10.78) * mm});
            skLineSegment(sketch, "E28.1.33.0", {"start": v(27.3, 12.45) * mm, "end": v(28.94, 13.69) * mm});
            skLineSegment(sketch, "E28.3.33.0", {"start": v(28.94, 13.69) * mm, "end": v(28.51, 14.53) * mm});
            skLineSegment(sketch, "E28.6.33.0", {"start": v(28.08, 15.37) * mm, "end": v(28.51, 14.53) * mm});
            skLineSegment(sketch, "E28.9.33.0", {"start": v(26.11, 14.77) * mm, "end": v(28.08, 15.37) * mm});
            skLineSegment(sketch, "E28.1.34.0", {"start": v(25.01, 16.57) * mm, "end": v(26.44, 18.05) * mm});
            skLineSegment(sketch, "E28.3.34.0", {"start": v(26.44, 18.05) * mm, "end": v(25.89, 18.8) * mm});
            skLineSegment(sketch, "E28.6.34.0", {"start": v(25.33, 19.57) * mm, "end": v(25.89, 18.8) * mm});
            skLineSegment(sketch, "E28.9.34.0", {"start": v(23.48, 18.67) * mm, "end": v(25.33, 19.57) * mm});
            skLineSegment(sketch, "E28.1.35.0", {"start": v(22.11, 20.27) * mm, "end": v(23.3, 21.96) * mm});
            skLineSegment(sketch, "E28.3.35.0", {"start": v(23.3, 21.96) * mm, "end": v(22.63, 22.63) * mm});
            skLineSegment(sketch, "E28.6.35.0", {"start": v(21.96, 23.3) * mm, "end": v(22.63, 22.63) * mm});
            skLineSegment(sketch, "E28.9.35.0", {"start": v(20.27, 22.11) * mm, "end": v(21.96, 23.3) * mm});
            skLineSegment(sketch, "E28.1.36.0", {"start": v(18.67, 23.48) * mm, "end": v(19.57, 25.33) * mm});
            skLineSegment(sketch, "E28.3.36.0", {"start": v(19.57, 25.33) * mm, "end": v(18.8, 25.89) * mm});
            skLineSegment(sketch, "E28.6.36.0", {"start": v(18.05, 26.44) * mm, "end": v(18.8, 25.89) * mm});
            skLineSegment(sketch, "E28.9.36.0", {"start": v(16.57, 25.01) * mm, "end": v(18.05, 26.44) * mm});
            skLineSegment(sketch, "E28.1.37.0", {"start": v(14.77, 26.11) * mm, "end": v(15.37, 28.08) * mm});
            skLineSegment(sketch, "E28.3.37.0", {"start": v(15.37, 28.08) * mm, "end": v(14.53, 28.51) * mm});
            skLineSegment(sketch, "E28.6.37.0", {"start": v(13.69, 28.94) * mm, "end": v(14.53, 28.51) * mm});
            skLineSegment(sketch, "E28.9.37.0", {"start": v(12.45, 27.3) * mm, "end": v(13.69, 28.94) * mm});
            skLineSegment(sketch, "E28.1.38.0", {"start": v(10.5, 28.1) * mm, "end": v(10.78, 30.14) * mm});
            skLineSegment(sketch, "E28.3.38.0", {"start": v(10.78, 30.14) * mm, "end": v(9.89, 30.43) * mm});
            skLineSegment(sketch, "E28.6.38.0", {"start": v(9, 30.73) * mm, "end": v(9.89, 30.43) * mm});
            skLineSegment(sketch, "E28.9.38.0", {"start": v(8.03, 28.9) * mm, "end": v(9, 30.73) * mm});
            skLineSegment(sketch, "E28.1.39.0", {"start": v(5.97, 29.4) * mm, "end": v(5.94, 31.46) * mm});
            skLineSegment(sketch, "E28.3.39.0", {"start": v(5.94, 31.46) * mm, "end": v(5, 31.6) * mm});
            skLineSegment(sketch, "E28.6.39.0", {"start": v(4.08, 31.75) * mm, "end": v(5, 31.6) * mm});
            skLineSegment(sketch, "E28.9.39.0", {"start": v(3.4, 29.8) * mm, "end": v(4.08, 31.75) * mm});
            skSolve(sketch);
        }
        {
            var Q0;
            Q0 = qSketchRegion(id + "F14", true);
            extrude(context, id + "F15", {"entities" : qUnion([Q0]), "operationType" : NewBodyOperationType.ADD, "depth" : 4 * mm, "offsetDistance" : 25 * mm});
        }
        {
            var Q0;
            Q0=makeQuery(id+"F7.opExtrude","CAP_FACE",FACE,{"disambiguationData":[OSD([sQuery(id+"F0.wireOp",EDGE,"E0")])],"isStart":false});
            var sketch = newSketch(context, id + "F16", { "sketchPlane" : qUnion([Q0])});
            skCircle(sketch, "E29", {"center": v(40, 0) * mm, "radius": 7.5 * mm});
            skLineSegment(sketch, "E30", {"start": v(40, 0) * mm, "end": v(40, 7.5) * mm, "construction": true});
            skLineSegment(sketch, "E31", {"start": v(38.68, 7.38) * mm, "end": v(39.06, 9.5) * mm});
            skLineSegment(sketch, "E32", {"start": v(39.06, 9.5) * mm, "end": v(40.94, 9.5) * mm});
            skLineSegment(sketch, "E33.MirrorCS", {"start": v(41.32, 7.38) * mm, "end": v(40.94, 9.5) * mm});
            skLineSegment(sketch, "E34.1.0", {"start": v(34.6, 5.2) * mm, "end": v(33.65, 7.13) * mm});
            skLineSegment(sketch, "E34.1.1", {"start": v(33.65, 7.13) * mm, "end": v(35.18, 8.24) * mm});
            skLineSegment(sketch, "E34.1.2", {"start": v(36.72, 6.75) * mm, "end": v(35.18, 8.24) * mm});
            skLineSegment(sketch, "E34.2.0", {"start": v(32.57, 1.03) * mm, "end": v(30.67, 2.04) * mm});
            skLineSegment(sketch, "E34.2.1", {"start": v(30.67, 2.04) * mm, "end": v(31.26, 3.83) * mm});
            skLineSegment(sketch, "E34.2.2", {"start": v(33.38, 3.53) * mm, "end": v(31.26, 3.83) * mm});
            skLineSegment(sketch, "E35.1.3.0", {"start": v(33.38, -3.53) * mm, "end": v(31.26, -3.83) * mm});
            skLineSegment(sketch, "E35.3.3.0", {"start": v(31.26, -3.83) * mm, "end": v(30.67, -2.04) * mm});
            skLineSegment(sketch, "E35.6.3.0", {"start": v(32.57, -1.03) * mm, "end": v(30.67, -2.04) * mm});
            skLineSegment(sketch, "E35.1.4.0", {"start": v(36.72, -6.75) * mm, "end": v(35.18, -8.24) * mm});
            skLineSegment(sketch, "E35.3.4.0", {"start": v(35.18, -8.24) * mm, "end": v(33.65, -7.13) * mm});
            skLineSegment(sketch, "E35.6.4.0", {"start": v(34.6, -5.2) * mm, "end": v(33.65, -7.13) * mm});
            skLineSegment(sketch, "E35.1.5.0", {"start": v(41.32, -7.38) * mm, "end": v(40.94, -9.5) * mm});
            skLineSegment(sketch, "E35.3.5.0", {"start": v(40.94, -9.5) * mm, "end": v(39.06, -9.5) * mm});
            skLineSegment(sketch, "E35.6.5.0", {"start": v(38.68, -7.38) * mm, "end": v(39.06, -9.5) * mm});
            skLineSegment(sketch, "E35.1.6.0", {"start": v(45.4, -5.2) * mm, "end": v(46.35, -7.13) * mm});
            skLineSegment(sketch, "E35.3.6.0", {"start": v(46.35, -7.13) * mm, "end": v(44.82, -8.24) * mm});
            skLineSegment(sketch, "E35.6.6.0", {"start": v(43.28, -6.75) * mm, "end": v(44.82, -8.24) * mm});
            skLineSegment(sketch, "E35.1.7.0", {"start": v(47.43, -1.03) * mm, "end": v(49.33, -2.04) * mm});
            skLineSegment(sketch, "E35.3.7.0", {"start": v(49.33, -2.04) * mm, "end": v(48.74, -3.83) * mm});
            skLineSegment(sketch, "E35.6.7.0", {"start": v(46.62, -3.53) * mm, "end": v(48.74, -3.83) * mm});
            skLineSegment(sketch, "E35.1.8.0", {"start": v(46.62, 3.53) * mm, "end": v(48.74, 3.83) * mm});
            skLineSegment(sketch, "E35.3.8.0", {"start": v(48.74, 3.83) * mm, "end": v(49.33, 2.04) * mm});
            skLineSegment(sketch, "E35.6.8.0", {"start": v(47.43, 1.03) * mm, "end": v(49.33, 2.04) * mm});
            skLineSegment(sketch, "E35.1.9.0", {"start": v(43.28, 6.75) * mm, "end": v(44.82, 8.24) * mm});
            skLineSegment(sketch, "E35.3.9.0", {"start": v(44.82, 8.24) * mm, "end": v(46.35, 7.13) * mm});
            skLineSegment(sketch, "E35.6.9.0", {"start": v(45.4, 5.2) * mm, "end": v(46.35, 7.13) * mm});
            skSolve(sketch);
        }
        {
            var Q0;
            Q0 = qSketchRegion(id + "F16", true);
            extrude(context, id + "F17", {"entities" : qUnion([Q0]), "operationType" : NewBodyOperationType.ADD, "depth" : 4 * mm, "offsetDistance" : 25 * mm});
        }
        {
            var Q0;
            Q0=makeQuery(id+"F17.opExtrude","CAP_FACE",FACE,{"disambiguationData":[OSD([sQuery(id+"F16.wireOp",EDGE,"E29"),sQuery(id+"F16.wireOp",EDGE,"E31"),sQuery(id+"F16.wireOp",EDGE,"E32"),sQuery(id+"F16.wireOp",EDGE,"E33.MirrorCS"),sQuery(id+"F16.wireOp",EDGE,"E34.1.0"),sQuery(id+"F16.wireOp",EDGE,"E34.1.1"),sQuery(id+"F16.wireOp",EDGE,"E34.1.2"),sQuery(id+"F16.wireOp",EDGE,"E34.2.0"),sQuery(id+"F16.wireOp",EDGE,"E34.2.1"),sQuery(id+"F16.wireOp",EDGE,"E34.2.2"),sQuery(id+"F16.wireOp",EDGE,"E35.1.3.0"),sQuery(id+"F16.wireOp",EDGE,"E35.3.3.0"),sQuery(id+"F16.wireOp",EDGE,"E35.6.3.0"),sQuery(id+"F16.wireOp",EDGE,"E35.1.4.0"),sQuery(id+"F16.wireOp",EDGE,"E35.3.4.0"),sQuery(id+"F16.wireOp",EDGE,"E35.6.4.0"),sQuery(id+"F16.wireOp",EDGE,"E35.1.5.0"),sQuery(id+"F16.wireOp",EDGE,"E35.3.5.0"),sQuery(id+"F16.wireOp",EDGE,"E35.6.5.0"),sQuery(id+"F16.wireOp",EDGE,"E35.1.6.0"),sQuery(id+"F16.wireOp",EDGE,"E35.3.6.0"),sQuery(id+"F16.wireOp",EDGE,"E35.6.6.0"),sQuery(id+"F16.wireOp",EDGE,"E35.1.7.0"),sQuery(id+"F16.wireOp",EDGE,"E35.3.7.0"),sQuery(id+"F16.wireOp",EDGE,"E35.6.7.0"),sQuery(id+"F16.wireOp",EDGE,"E35.1.8.0"),sQuery(id+"F16.wireOp",EDGE,"E35.3.8.0"),sQuery(id+"F16.wireOp",EDGE,"E35.6.8.0"),sQuery(id+"F16.wireOp",EDGE,"E35.1.9.0"),sQuery(id+"F16.wireOp",EDGE,"E35.3.9.0"),sQuery(id+"F16.wireOp",EDGE,"E35.6.9.0")])],"isStart":false});
            var sketch = newSketch(context, id + "F18", { "sketchPlane" : qUnion([Q0])});
            skCircle(sketch, "E36.0", {"center": v(40, 0) * mm, "radius": 3 * mm});
            skSolve(sketch);
        }
        {
            var Q0;
            Q0 = qSketchRegion(id + "F18", true);
            extrude(context, id + "F19", {"entities" : qUnion([Q0]), "operationType" : NewBodyOperationType.ADD, "depth" : 2 * mm, "offsetDistance" : 25 * mm});
        }
        {
            var Q0;
            Q0=makeQuery(id+"F19.opExtrude","CAP_FACE",FACE,{"disambiguationData":[OSD([sQuery(id+"F18.wireOp",EDGE,"E36.0")])],"isStart":false});
            var sketch = newSketch(context, id + "F20", { "sketchPlane" : qUnion([Q0])});
            skCircle(sketch, "E37", {"center": v(0, 0) * mm, "radius": 98 * mm});
            skCircle(sketch, "E38.0", {"center": v(0, 0) * mm, "radius": 5 * mm});
            skSolve(sketch);
        }
        {
            var Q0;
            Q0 = qSketchRegion(id + "F20", true);
            extrude(context, id + "F21", {"entities" : qUnion([Q0]), "depth" : 1 * mm, "offsetDistance" : 25 * mm});
        }
        {
            var Q0;
            Q0=makeQuery(id+"F21.opExtrude","SWEPT_BODY",BODY,{"disambiguationData":[OSD([sQuery(id+"F20.wireOp",EDGE,"E37"),sQuery(id+"F20.wireOp",EDGE,"E38.0")])]});
            var Q1;
            Q1=makeQuery(id+"F1.opExtrude","SWEPT_BODY",BODY,{"disambiguationData":[OSD([sQuery(id+"F0.wireOp",EDGE,"E0")])]});
            booleanBodies(context, id + "F22", {"operationType" : BooleanOperationType.SUBTRACTION, "tools" : qUnion([Q0]), "targets" : qUnion([Q1]), "keepTools" : true});
        }
        {
            var Q0;
            Q0=makeQuery(id+"F21.opExtrude","CAP_FACE",FACE,{"disambiguationData":[OSD([sQuery(id+"F20.wireOp",EDGE,"E37"),sQuery(id+"F20.wireOp",EDGE,"E38.0")])],"isStart":true});
            var sketch = newSketch(context, id + "F23", { "sketchPlane" : qUnion([Q0])});
            skCircle(sketch, "E39.0", {"center": v(-40, 0) * mm, "radius": 3 * mm});
            skCircle(sketch, "E40", {"center": v(-40, 0) * mm, "radius": 5 * mm});
            skSolve(sketch);
        }
        {
            var Q0;
            Q0 = qSketchRegion(id + "F23", true);
            extrude(context, id + "F24", {"entities" : qUnion([Q0]), "operationType" : NewBodyOperationType.ADD, "endBound" : BoundingType.UP_TO_NEXT, "depth" : 25 * mm, "offsetDistance" : 25 * mm});
        }
        {
            var Q0;
            Q0=makeQuery(id+"F21.opExtrude","CAP_FACE",FACE,{"disambiguationData":[OSD([sQuery(id+"F20.wireOp",EDGE,"E37"),sQuery(id+"F20.wireOp",EDGE,"E38.0")])],"isStart":false});
            var sketch = newSketch(context, id + "F25", { "sketchPlane" : qUnion([Q0])});
            skLineSegment(sketch, "E41.bottom", {"start": v(1.5, 71) * mm, "end": v(-1.5, 71) * mm});
            skLineSegment(sketch, "E41.top", {"start": v(1.5, 91) * mm, "end": v(-1.5, 91) * mm});
            skLineSegment(sketch, "E41.left", {"start": v(1.5, 71) * mm, "end": v(1.5, 91) * mm});
            skLineSegment(sketch, "E41.right", {"start": v(-1.5, 71) * mm, "end": v(-1.5, 91) * mm});
            skPoint(sketch, "E41.middle", {"position": v(0, 81) * mm});
            skLineSegment(sketch, "E42.1.0", {"start": v(-44.2, 79.56) * mm, "end": v(-46.8, 78.06) * mm});
            skLineSegment(sketch, "E42.1.1", {"start": v(-36.8, 60.74) * mm, "end": v(-46.8, 78.06) * mm});
            skLineSegment(sketch, "E42.1.2", {"start": v(-34.2, 62.24) * mm, "end": v(-44.2, 79.56) * mm});
            skLineSegment(sketch, "E42.1.3", {"start": v(-34.2, 62.24) * mm, "end": v(-36.8, 60.74) * mm});
            skLineSegment(sketch, "E42.2.0", {"start": v(-78.06, 46.8) * mm, "end": v(-79.56, 44.2) * mm});
            skLineSegment(sketch, "E42.2.1", {"start": v(-62.24, 34.2) * mm, "end": v(-79.56, 44.2) * mm});
            skLineSegment(sketch, "E42.2.2", {"start": v(-60.74, 36.8) * mm, "end": v(-78.06, 46.8) * mm});
            skLineSegment(sketch, "E42.2.3", {"start": v(-60.74, 36.8) * mm, "end": v(-62.24, 34.2) * mm});
            skPoint(sketch, "E42.center", {"position": v(0, 0) * mm});
            skLineSegment(sketch, "E43.2.3.0", {"start": v(-91, 1.5) * mm, "end": v(-91, -1.5) * mm});
            skLineSegment(sketch, "E43.3.3.0", {"start": v(-71, -1.5) * mm, "end": v(-91, -1.5) * mm});
            skLineSegment(sketch, "E43.6.3.0", {"start": v(-71, 1.5) * mm, "end": v(-91, 1.5) * mm});
            skLineSegment(sketch, "E43.9.3.0", {"start": v(-71, 1.5) * mm, "end": v(-71, -1.5) * mm});
            skLineSegment(sketch, "E43.2.4.0", {"start": v(-79.56, -44.2) * mm, "end": v(-78.06, -46.8) * mm});
            skLineSegment(sketch, "E43.3.4.0", {"start": v(-60.74, -36.8) * mm, "end": v(-78.06, -46.8) * mm});
            skLineSegment(sketch, "E43.6.4.0", {"start": v(-62.24, -34.2) * mm, "end": v(-79.56, -44.2) * mm});
            skLineSegment(sketch, "E43.9.4.0", {"start": v(-62.24, -34.2) * mm, "end": v(-60.74, -36.8) * mm});
            skLineSegment(sketch, "E43.2.5.0", {"start": v(-46.8, -78.06) * mm, "end": v(-44.2, -79.56) * mm});
            skLineSegment(sketch, "E43.3.5.0", {"start": v(-34.2, -62.24) * mm, "end": v(-44.2, -79.56) * mm});
            skLineSegment(sketch, "E43.6.5.0", {"start": v(-36.8, -60.74) * mm, "end": v(-46.8, -78.06) * mm});
            skLineSegment(sketch, "E43.9.5.0", {"start": v(-36.8, -60.74) * mm, "end": v(-34.2, -62.24) * mm});
            skLineSegment(sketch, "E43.2.6.0", {"start": v(-1.5, -91) * mm, "end": v(1.5, -91) * mm});
            skLineSegment(sketch, "E43.3.6.0", {"start": v(1.5, -71) * mm, "end": v(1.5, -91) * mm});
            skLineSegment(sketch, "E43.6.6.0", {"start": v(-1.5, -71) * mm, "end": v(-1.5, -91) * mm});
            skLineSegment(sketch, "E43.9.6.0", {"start": v(-1.5, -71) * mm, "end": v(1.5, -71) * mm});
            skLineSegment(sketch, "E43.2.7.0", {"start": v(44.2, -79.56) * mm, "end": v(46.8, -78.06) * mm});
            skLineSegment(sketch, "E43.3.7.0", {"start": v(36.8, -60.74) * mm, "end": v(46.8, -78.06) * mm});
            skLineSegment(sketch, "E43.6.7.0", {"start": v(34.2, -62.24) * mm, "end": v(44.2, -79.56) * mm});
            skLineSegment(sketch, "E43.9.7.0", {"start": v(34.2, -62.24) * mm, "end": v(36.8, -60.74) * mm});
            skLineSegment(sketch, "E43.2.8.0", {"start": v(78.06, -46.8) * mm, "end": v(79.56, -44.2) * mm});
            skLineSegment(sketch, "E43.3.8.0", {"start": v(62.24, -34.2) * mm, "end": v(79.56, -44.2) * mm});
            skLineSegment(sketch, "E43.6.8.0", {"start": v(60.74, -36.8) * mm, "end": v(78.06, -46.8) * mm});
            skLineSegment(sketch, "E43.9.8.0", {"start": v(60.74, -36.8) * mm, "end": v(62.24, -34.2) * mm});
            skLineSegment(sketch, "E43.2.9.0", {"start": v(91, -1.5) * mm, "end": v(91, 1.5) * mm});
            skLineSegment(sketch, "E43.3.9.0", {"start": v(71, 1.5) * mm, "end": v(91, 1.5) * mm});
            skLineSegment(sketch, "E43.6.9.0", {"start": v(71, -1.5) * mm, "end": v(91, -1.5) * mm});
            skLineSegment(sketch, "E43.9.9.0", {"start": v(71, -1.5) * mm, "end": v(71, 1.5) * mm});
            skLineSegment(sketch, "E43.2.10.0", {"start": v(79.56, 44.2) * mm, "end": v(78.06, 46.8) * mm});
            skLineSegment(sketch, "E43.3.10.0", {"start": v(60.74, 36.8) * mm, "end": v(78.06, 46.8) * mm});
            skLineSegment(sketch, "E43.6.10.0", {"start": v(62.24, 34.2) * mm, "end": v(79.56, 44.2) * mm});
            skLineSegment(sketch, "E43.9.10.0", {"start": v(62.24, 34.2) * mm, "end": v(60.74, 36.8) * mm});
            skLineSegment(sketch, "E43.2.11.0", {"start": v(46.8, 78.06) * mm, "end": v(44.2, 79.56) * mm});
            skLineSegment(sketch, "E43.3.11.0", {"start": v(34.2, 62.24) * mm, "end": v(44.2, 79.56) * mm});
            skLineSegment(sketch, "E43.6.11.0", {"start": v(36.8, 60.74) * mm, "end": v(46.8, 78.06) * mm});
            skLineSegment(sketch, "E43.9.11.0", {"start": v(36.8, 60.74) * mm, "end": v(34.2, 62.24) * mm});
            skSolve(sketch);
        }
        {
            var Q0;
            Q0 = qSketchRegion(id + "F25", true);
            extrude(context, id + "F26", {"entities" : qUnion([Q0]), "operationType" : NewBodyOperationType.REMOVE, "oppositeDirection" : true, "depth" : 0.5 * mm, "offsetDistance" : 25 * mm});
        }
        {
            var Q0;
            Q0=makeQuery(id+"F21.opExtrude","CAP_FACE",FACE,{"disambiguationData":[OSD([sQuery(id+"F20.wireOp",EDGE,"E37"),sQuery(id+"F20.wireOp",EDGE,"E38.0")])],"isStart":false});
            var sketch = newSketch(context, id + "F27", { "sketchPlane" : qUnion([Q0])});
            skLineSegment(sketch, "E44.bottom", {"start": v(0.75, 90.5) * mm, "end": v(-0.75, 90.5) * mm});
            skLineSegment(sketch, "E44.top", {"start": v(0.75, 78.5) * mm, "end": v(-0.75, 78.5) * mm});
            skLineSegment(sketch, "E44.left", {"start": v(0.75, 90.5) * mm, "end": v(0.75, 78.5) * mm});
            skLineSegment(sketch, "E44.right", {"start": v(-0.75, 90.5) * mm, "end": v(-0.75, 78.5) * mm});
            skPoint(sketch, "E44.middle", {"position": v(0, 84.5) * mm});
            skLineSegment(sketch, "E45.1.0", {"start": v(-7.46, 78.15) * mm, "end": v(-8.95, 78) * mm});
            skLineSegment(sketch, "E45.1.1", {"start": v(-10.2, 89.93) * mm, "end": v(-8.95, 78) * mm});
            skLineSegment(sketch, "E45.1.2", {"start": v(-8.71, 90.08) * mm, "end": v(-7.46, 78.15) * mm});
            skLineSegment(sketch, "E45.1.3", {"start": v(-8.71, 90.08) * mm, "end": v(-10.2, 89.93) * mm});
            skLineSegment(sketch, "E45.2.0", {"start": v(-15.59, 76.94) * mm, "end": v(-17.05, 76.63) * mm});
            skLineSegment(sketch, "E45.2.1", {"start": v(-19.55, 88.37) * mm, "end": v(-17.05, 76.63) * mm});
            skLineSegment(sketch, "E45.2.2", {"start": v(-18.08, 88.68) * mm, "end": v(-15.59, 76.94) * mm});
            skLineSegment(sketch, "E45.2.3", {"start": v(-18.08, 88.68) * mm, "end": v(-19.55, 88.37) * mm});
            skPoint(sketch, "E45.center", {"position": v(0, 0) * mm});
            skLineSegment(sketch, "E46.2.3.0", {"start": v(-23.54, 74.89) * mm, "end": v(-24.97, 74.43) * mm});
            skLineSegment(sketch, "E46.3.3.0", {"start": v(-28.68, 85.84) * mm, "end": v(-24.97, 74.43) * mm});
            skLineSegment(sketch, "E46.6.3.0", {"start": v(-27.25, 86.3) * mm, "end": v(-23.54, 74.89) * mm});
            skLineSegment(sketch, "E46.9.3.0", {"start": v(-27.25, 86.3) * mm, "end": v(-28.68, 85.84) * mm});
            skLineSegment(sketch, "E46.2.4.0", {"start": v(-31.24, 72.02) * mm, "end": v(-32.61, 71.4) * mm});
            skLineSegment(sketch, "E46.3.4.0", {"start": v(-37.5, 82.37) * mm, "end": v(-32.61, 71.4) * mm});
            skLineSegment(sketch, "E46.6.4.0", {"start": v(-36.12, 82.98) * mm, "end": v(-31.24, 72.02) * mm});
            skLineSegment(sketch, "E46.9.4.0", {"start": v(-36.12, 82.98) * mm, "end": v(-37.5, 82.37) * mm});
            skLineSegment(sketch, "E46.2.5.0", {"start": v(-38.6, 68.36) * mm, "end": v(-39.9, 67.6) * mm});
            skLineSegment(sketch, "E46.3.5.0", {"start": v(-45.9, 78) * mm, "end": v(-39.9, 67.6) * mm});
            skLineSegment(sketch, "E46.6.5.0", {"start": v(-44.6, 78.75) * mm, "end": v(-38.6, 68.36) * mm});
            skLineSegment(sketch, "E46.9.5.0", {"start": v(-44.6, 78.75) * mm, "end": v(-45.9, 78) * mm});
            skLineSegment(sketch, "E46.2.6.0", {"start": v(-45.53, 63.95) * mm, "end": v(-46.75, 63.07) * mm});
            skLineSegment(sketch, "E46.3.6.0", {"start": v(-53.8, 72.78) * mm, "end": v(-46.75, 63.07) * mm});
            skLineSegment(sketch, "E46.6.6.0", {"start": v(-52.59, 73.66) * mm, "end": v(-45.53, 63.95) * mm});
            skLineSegment(sketch, "E46.9.6.0", {"start": v(-52.59, 73.66) * mm, "end": v(-53.8, 72.78) * mm});
            skLineSegment(sketch, "E46.2.7.0", {"start": v(-51.97, 58.84) * mm, "end": v(-53.08, 57.84) * mm});
            skLineSegment(sketch, "E46.3.7.0", {"start": v(-61.11, 66.75) * mm, "end": v(-53.08, 57.84) * mm});
            skLineSegment(sketch, "E46.6.7.0", {"start": v(-60, 67.76) * mm, "end": v(-51.97, 58.84) * mm});
            skLineSegment(sketch, "E46.9.7.0", {"start": v(-60, 67.76) * mm, "end": v(-61.11, 66.75) * mm});
            skLineSegment(sketch, "E46.2.8.0", {"start": v(-57.84, 53.08) * mm, "end": v(-58.84, 51.97) * mm});
            skLineSegment(sketch, "E46.3.8.0", {"start": v(-67.76, 60) * mm, "end": v(-58.84, 51.97) * mm});
            skLineSegment(sketch, "E46.6.8.0", {"start": v(-66.75, 61.11) * mm, "end": v(-57.84, 53.08) * mm});
            skLineSegment(sketch, "E46.9.8.0", {"start": v(-66.75, 61.11) * mm, "end": v(-67.76, 60) * mm});
            skLineSegment(sketch, "E46.2.9.0", {"start": v(-63.07, 46.75) * mm, "end": v(-63.95, 45.53) * mm});
            skLineSegment(sketch, "E46.3.9.0", {"start": v(-73.66, 52.59) * mm, "end": v(-63.95, 45.53) * mm});
            skLineSegment(sketch, "E46.6.9.0", {"start": v(-72.78, 53.8) * mm, "end": v(-63.07, 46.75) * mm});
            skLineSegment(sketch, "E46.9.9.0", {"start": v(-72.78, 53.8) * mm, "end": v(-73.66, 52.59) * mm});
            skLineSegment(sketch, "E46.2.10.0", {"start": v(-67.6, 39.9) * mm, "end": v(-68.36, 38.6) * mm});
            skLineSegment(sketch, "E46.3.10.0", {"start": v(-78.75, 44.6) * mm, "end": v(-68.36, 38.6) * mm});
            skLineSegment(sketch, "E46.6.10.0", {"start": v(-78, 45.9) * mm, "end": v(-67.6, 39.9) * mm});
            skLineSegment(sketch, "E46.9.10.0", {"start": v(-78, 45.9) * mm, "end": v(-78.75, 44.6) * mm});
            skLineSegment(sketch, "E46.2.11.0", {"start": v(-71.4, 32.61) * mm, "end": v(-72.02, 31.24) * mm});
            skLineSegment(sketch, "E46.3.11.0", {"start": v(-82.98, 36.12) * mm, "end": v(-72.02, 31.24) * mm});
            skLineSegment(sketch, "E46.6.11.0", {"start": v(-82.37, 37.5) * mm, "end": v(-71.4, 32.61) * mm});
            skLineSegment(sketch, "E46.9.11.0", {"start": v(-82.37, 37.5) * mm, "end": v(-82.98, 36.12) * mm});
            skLineSegment(sketch, "E46.2.12.0", {"start": v(-74.43, 24.97) * mm, "end": v(-74.89, 23.54) * mm});
            skLineSegment(sketch, "E46.3.12.0", {"start": v(-86.3, 27.25) * mm, "end": v(-74.89, 23.54) * mm});
            skLineSegment(sketch, "E46.6.12.0", {"start": v(-85.84, 28.68) * mm, "end": v(-74.43, 24.97) * mm});
            skLineSegment(sketch, "E46.9.12.0", {"start": v(-85.84, 28.68) * mm, "end": v(-86.3, 27.25) * mm});
            skLineSegment(sketch, "E46.2.13.0", {"start": v(-76.63, 17.05) * mm, "end": v(-76.94, 15.59) * mm});
            skLineSegment(sketch, "E46.3.13.0", {"start": v(-88.68, 18.08) * mm, "end": v(-76.94, 15.59) * mm});
            skLineSegment(sketch, "E46.6.13.0", {"start": v(-88.37, 19.55) * mm, "end": v(-76.63, 17.05) * mm});
            skLineSegment(sketch, "E46.9.13.0", {"start": v(-88.37, 19.55) * mm, "end": v(-88.68, 18.08) * mm});
            skLineSegment(sketch, "E46.2.14.0", {"start": v(-78, 8.95) * mm, "end": v(-78.15, 7.46) * mm});
            skLineSegment(sketch, "E46.3.14.0", {"start": v(-90.08, 8.71) * mm, "end": v(-78.15, 7.46) * mm});
            skLineSegment(sketch, "E46.6.14.0", {"start": v(-89.93, 10.2) * mm, "end": v(-78, 8.95) * mm});
            skLineSegment(sketch, "E46.9.14.0", {"start": v(-89.93, 10.2) * mm, "end": v(-90.08, 8.71) * mm});
            skLineSegment(sketch, "E46.2.15.0", {"start": v(-78.5, 0.75) * mm, "end": v(-78.5, -0.75) * mm});
            skLineSegment(sketch, "E46.3.15.0", {"start": v(-90.5, -0.75) * mm, "end": v(-78.5, -0.75) * mm});
            skLineSegment(sketch, "E46.6.15.0", {"start": v(-90.5, 0.75) * mm, "end": v(-78.5, 0.75) * mm});
            skLineSegment(sketch, "E46.9.15.0", {"start": v(-90.5, 0.75) * mm, "end": v(-90.5, -0.75) * mm});
            skLineSegment(sketch, "E46.2.16.0", {"start": v(-78.15, -7.46) * mm, "end": v(-78, -8.95) * mm});
            skLineSegment(sketch, "E46.3.16.0", {"start": v(-89.93, -10.2) * mm, "end": v(-78, -8.95) * mm});
            skLineSegment(sketch, "E46.6.16.0", {"start": v(-90.08, -8.71) * mm, "end": v(-78.15, -7.46) * mm});
            skLineSegment(sketch, "E46.9.16.0", {"start": v(-90.08, -8.71) * mm, "end": v(-89.93, -10.2) * mm});
            skLineSegment(sketch, "E46.2.17.0", {"start": v(-76.94, -15.59) * mm, "end": v(-76.63, -17.05) * mm});
            skLineSegment(sketch, "E46.3.17.0", {"start": v(-88.37, -19.55) * mm, "end": v(-76.63, -17.05) * mm});
            skLineSegment(sketch, "E46.6.17.0", {"start": v(-88.68, -18.08) * mm, "end": v(-76.94, -15.59) * mm});
            skLineSegment(sketch, "E46.9.17.0", {"start": v(-88.68, -18.08) * mm, "end": v(-88.37, -19.55) * mm});
            skLineSegment(sketch, "E46.2.18.0", {"start": v(-74.89, -23.54) * mm, "end": v(-74.43, -24.97) * mm});
            skLineSegment(sketch, "E46.3.18.0", {"start": v(-85.84, -28.68) * mm, "end": v(-74.43, -24.97) * mm});
            skLineSegment(sketch, "E46.6.18.0", {"start": v(-86.3, -27.25) * mm, "end": v(-74.89, -23.54) * mm});
            skLineSegment(sketch, "E46.9.18.0", {"start": v(-86.3, -27.25) * mm, "end": v(-85.84, -28.68) * mm});
            skLineSegment(sketch, "E46.2.19.0", {"start": v(-72.02, -31.24) * mm, "end": v(-71.4, -32.61) * mm});
            skLineSegment(sketch, "E46.3.19.0", {"start": v(-82.37, -37.5) * mm, "end": v(-71.4, -32.61) * mm});
            skLineSegment(sketch, "E46.6.19.0", {"start": v(-82.98, -36.12) * mm, "end": v(-72.02, -31.24) * mm});
            skLineSegment(sketch, "E46.9.19.0", {"start": v(-82.98, -36.12) * mm, "end": v(-82.37, -37.5) * mm});
            skLineSegment(sketch, "E46.2.20.0", {"start": v(-68.36, -38.6) * mm, "end": v(-67.6, -39.9) * mm});
            skLineSegment(sketch, "E46.3.20.0", {"start": v(-78, -45.9) * mm, "end": v(-67.6, -39.9) * mm});
            skLineSegment(sketch, "E46.6.20.0", {"start": v(-78.75, -44.6) * mm, "end": v(-68.36, -38.6) * mm});
            skLineSegment(sketch, "E46.9.20.0", {"start": v(-78.75, -44.6) * mm, "end": v(-78, -45.9) * mm});
            skLineSegment(sketch, "E46.2.21.0", {"start": v(-63.95, -45.53) * mm, "end": v(-63.07, -46.75) * mm});
            skLineSegment(sketch, "E46.3.21.0", {"start": v(-72.78, -53.8) * mm, "end": v(-63.07, -46.75) * mm});
            skLineSegment(sketch, "E46.6.21.0", {"start": v(-73.66, -52.59) * mm, "end": v(-63.95, -45.53) * mm});
            skLineSegment(sketch, "E46.9.21.0", {"start": v(-73.66, -52.59) * mm, "end": v(-72.78, -53.8) * mm});
            skLineSegment(sketch, "E46.2.22.0", {"start": v(-58.84, -51.97) * mm, "end": v(-57.84, -53.08) * mm});
            skLineSegment(sketch, "E46.3.22.0", {"start": v(-66.75, -61.11) * mm, "end": v(-57.84, -53.08) * mm});
            skLineSegment(sketch, "E46.6.22.0", {"start": v(-67.76, -60) * mm, "end": v(-58.84, -51.97) * mm});
            skLineSegment(sketch, "E46.9.22.0", {"start": v(-67.76, -60) * mm, "end": v(-66.75, -61.11) * mm});
            skLineSegment(sketch, "E46.2.23.0", {"start": v(-53.08, -57.84) * mm, "end": v(-51.97, -58.84) * mm});
            skLineSegment(sketch, "E46.3.23.0", {"start": v(-60, -67.76) * mm, "end": v(-51.97, -58.84) * mm});
            skLineSegment(sketch, "E46.6.23.0", {"start": v(-61.11, -66.75) * mm, "end": v(-53.08, -57.84) * mm});
            skLineSegment(sketch, "E46.9.23.0", {"start": v(-61.11, -66.75) * mm, "end": v(-60, -67.76) * mm});
            skLineSegment(sketch, "E46.2.24.0", {"start": v(-46.75, -63.07) * mm, "end": v(-45.53, -63.95) * mm});
            skLineSegment(sketch, "E46.3.24.0", {"start": v(-52.59, -73.66) * mm, "end": v(-45.53, -63.95) * mm});
            skLineSegment(sketch, "E46.6.24.0", {"start": v(-53.8, -72.78) * mm, "end": v(-46.75, -63.07) * mm});
            skLineSegment(sketch, "E46.9.24.0", {"start": v(-53.8, -72.78) * mm, "end": v(-52.59, -73.66) * mm});
            skLineSegment(sketch, "E46.2.25.0", {"start": v(-39.9, -67.6) * mm, "end": v(-38.6, -68.36) * mm});
            skLineSegment(sketch, "E46.3.25.0", {"start": v(-44.6, -78.75) * mm, "end": v(-38.6, -68.36) * mm});
            skLineSegment(sketch, "E46.6.25.0", {"start": v(-45.9, -78) * mm, "end": v(-39.9, -67.6) * mm});
            skLineSegment(sketch, "E46.9.25.0", {"start": v(-45.9, -78) * mm, "end": v(-44.6, -78.75) * mm});
            skLineSegment(sketch, "E46.2.26.0", {"start": v(-32.61, -71.4) * mm, "end": v(-31.24, -72.02) * mm});
            skLineSegment(sketch, "E46.3.26.0", {"start": v(-36.12, -82.98) * mm, "end": v(-31.24, -72.02) * mm});
            skLineSegment(sketch, "E46.6.26.0", {"start": v(-37.5, -82.37) * mm, "end": v(-32.61, -71.4) * mm});
            skLineSegment(sketch, "E46.9.26.0", {"start": v(-37.5, -82.37) * mm, "end": v(-36.12, -82.98) * mm});
            skLineSegment(sketch, "E46.2.27.0", {"start": v(-24.97, -74.43) * mm, "end": v(-23.54, -74.89) * mm});
            skLineSegment(sketch, "E46.3.27.0", {"start": v(-27.25, -86.3) * mm, "end": v(-23.54, -74.89) * mm});
            skLineSegment(sketch, "E46.6.27.0", {"start": v(-28.68, -85.84) * mm, "end": v(-24.97, -74.43) * mm});
            skLineSegment(sketch, "E46.9.27.0", {"start": v(-28.68, -85.84) * mm, "end": v(-27.25, -86.3) * mm});
            skLineSegment(sketch, "E46.2.28.0", {"start": v(-17.05, -76.63) * mm, "end": v(-15.59, -76.94) * mm});
            skLineSegment(sketch, "E46.3.28.0", {"start": v(-18.08, -88.68) * mm, "end": v(-15.59, -76.94) * mm});
            skLineSegment(sketch, "E46.6.28.0", {"start": v(-19.55, -88.37) * mm, "end": v(-17.05, -76.63) * mm});
            skLineSegment(sketch, "E46.9.28.0", {"start": v(-19.55, -88.37) * mm, "end": v(-18.08, -88.68) * mm});
            skLineSegment(sketch, "E46.2.29.0", {"start": v(-8.95, -78) * mm, "end": v(-7.46, -78.15) * mm});
            skLineSegment(sketch, "E46.3.29.0", {"start": v(-8.71, -90.08) * mm, "end": v(-7.46, -78.15) * mm});
            skLineSegment(sketch, "E46.6.29.0", {"start": v(-10.2, -89.93) * mm, "end": v(-8.95, -78) * mm});
            skLineSegment(sketch, "E46.9.29.0", {"start": v(-10.2, -89.93) * mm, "end": v(-8.71, -90.08) * mm});
            skLineSegment(sketch, "E46.2.30.0", {"start": v(-0.75, -78.5) * mm, "end": v(0.75, -78.5) * mm});
            skLineSegment(sketch, "E46.3.30.0", {"start": v(0.75, -90.5) * mm, "end": v(0.75, -78.5) * mm});
            skLineSegment(sketch, "E46.6.30.0", {"start": v(-0.75, -90.5) * mm, "end": v(-0.75, -78.5) * mm});
            skLineSegment(sketch, "E46.9.30.0", {"start": v(-0.75, -90.5) * mm, "end": v(0.75, -90.5) * mm});
            skLineSegment(sketch, "E46.2.31.0", {"start": v(7.46, -78.15) * mm, "end": v(8.95, -78) * mm});
            skLineSegment(sketch, "E46.3.31.0", {"start": v(10.2, -89.93) * mm, "end": v(8.95, -78) * mm});
            skLineSegment(sketch, "E46.6.31.0", {"start": v(8.71, -90.08) * mm, "end": v(7.46, -78.15) * mm});
            skLineSegment(sketch, "E46.9.31.0", {"start": v(8.71, -90.08) * mm, "end": v(10.2, -89.93) * mm});
            skLineSegment(sketch, "E46.2.32.0", {"start": v(15.59, -76.94) * mm, "end": v(17.05, -76.63) * mm});
            skLineSegment(sketch, "E46.3.32.0", {"start": v(19.55, -88.37) * mm, "end": v(17.05, -76.63) * mm});
            skLineSegment(sketch, "E46.6.32.0", {"start": v(18.08, -88.68) * mm, "end": v(15.59, -76.94) * mm});
            skLineSegment(sketch, "E46.9.32.0", {"start": v(18.08, -88.68) * mm, "end": v(19.55, -88.37) * mm});
            skLineSegment(sketch, "E46.2.33.0", {"start": v(23.54, -74.89) * mm, "end": v(24.97, -74.43) * mm});
            skLineSegment(sketch, "E46.3.33.0", {"start": v(28.68, -85.84) * mm, "end": v(24.97, -74.43) * mm});
            skLineSegment(sketch, "E46.6.33.0", {"start": v(27.25, -86.3) * mm, "end": v(23.54, -74.89) * mm});
            skLineSegment(sketch, "E46.9.33.0", {"start": v(27.25, -86.3) * mm, "end": v(28.68, -85.84) * mm});
            skLineSegment(sketch, "E46.2.34.0", {"start": v(31.24, -72.02) * mm, "end": v(32.61, -71.4) * mm});
            skLineSegment(sketch, "E46.3.34.0", {"start": v(37.5, -82.37) * mm, "end": v(32.61, -71.4) * mm});
            skLineSegment(sketch, "E46.6.34.0", {"start": v(36.12, -82.98) * mm, "end": v(31.24, -72.02) * mm});
            skLineSegment(sketch, "E46.9.34.0", {"start": v(36.12, -82.98) * mm, "end": v(37.5, -82.37) * mm});
            skLineSegment(sketch, "E46.2.35.0", {"start": v(38.6, -68.36) * mm, "end": v(39.9, -67.6) * mm});
            skLineSegment(sketch, "E46.3.35.0", {"start": v(45.9, -78) * mm, "end": v(39.9, -67.6) * mm});
            skLineSegment(sketch, "E46.6.35.0", {"start": v(44.6, -78.75) * mm, "end": v(38.6, -68.36) * mm});
            skLineSegment(sketch, "E46.9.35.0", {"start": v(44.6, -78.75) * mm, "end": v(45.9, -78) * mm});
            skLineSegment(sketch, "E46.2.36.0", {"start": v(45.53, -63.95) * mm, "end": v(46.75, -63.07) * mm});
            skLineSegment(sketch, "E46.3.36.0", {"start": v(53.8, -72.78) * mm, "end": v(46.75, -63.07) * mm});
            skLineSegment(sketch, "E46.6.36.0", {"start": v(52.59, -73.66) * mm, "end": v(45.53, -63.95) * mm});
            skLineSegment(sketch, "E46.9.36.0", {"start": v(52.59, -73.66) * mm, "end": v(53.8, -72.78) * mm});
            skLineSegment(sketch, "E46.2.37.0", {"start": v(51.97, -58.84) * mm, "end": v(53.08, -57.84) * mm});
            skLineSegment(sketch, "E46.3.37.0", {"start": v(61.11, -66.75) * mm, "end": v(53.08, -57.84) * mm});
            skLineSegment(sketch, "E46.6.37.0", {"start": v(60, -67.76) * mm, "end": v(51.97, -58.84) * mm});
            skLineSegment(sketch, "E46.9.37.0", {"start": v(60, -67.76) * mm, "end": v(61.11, -66.75) * mm});
            skLineSegment(sketch, "E46.2.38.0", {"start": v(57.84, -53.08) * mm, "end": v(58.84, -51.97) * mm});
            skLineSegment(sketch, "E46.3.38.0", {"start": v(67.76, -60) * mm, "end": v(58.84, -51.97) * mm});
            skLineSegment(sketch, "E46.6.38.0", {"start": v(66.75, -61.11) * mm, "end": v(57.84, -53.08) * mm});
            skLineSegment(sketch, "E46.9.38.0", {"start": v(66.75, -61.11) * mm, "end": v(67.76, -60) * mm});
            skLineSegment(sketch, "E46.2.39.0", {"start": v(63.07, -46.75) * mm, "end": v(63.95, -45.53) * mm});
            skLineSegment(sketch, "E46.3.39.0", {"start": v(73.66, -52.59) * mm, "end": v(63.95, -45.53) * mm});
            skLineSegment(sketch, "E46.6.39.0", {"start": v(72.78, -53.8) * mm, "end": v(63.07, -46.75) * mm});
            skLineSegment(sketch, "E46.9.39.0", {"start": v(72.78, -53.8) * mm, "end": v(73.66, -52.59) * mm});
            skLineSegment(sketch, "E46.2.40.0", {"start": v(67.6, -39.9) * mm, "end": v(68.36, -38.6) * mm});
            skLineSegment(sketch, "E46.3.40.0", {"start": v(78.75, -44.6) * mm, "end": v(68.36, -38.6) * mm});
            skLineSegment(sketch, "E46.6.40.0", {"start": v(78, -45.9) * mm, "end": v(67.6, -39.9) * mm});
            skLineSegment(sketch, "E46.9.40.0", {"start": v(78, -45.9) * mm, "end": v(78.75, -44.6) * mm});
            skLineSegment(sketch, "E46.2.41.0", {"start": v(71.4, -32.61) * mm, "end": v(72.02, -31.24) * mm});
            skLineSegment(sketch, "E46.3.41.0", {"start": v(82.98, -36.12) * mm, "end": v(72.02, -31.24) * mm});
            skLineSegment(sketch, "E46.6.41.0", {"start": v(82.37, -37.5) * mm, "end": v(71.4, -32.61) * mm});
            skLineSegment(sketch, "E46.9.41.0", {"start": v(82.37, -37.5) * mm, "end": v(82.98, -36.12) * mm});
            skLineSegment(sketch, "E46.2.42.0", {"start": v(74.43, -24.97) * mm, "end": v(74.89, -23.54) * mm});
            skLineSegment(sketch, "E46.3.42.0", {"start": v(86.3, -27.25) * mm, "end": v(74.89, -23.54) * mm});
            skLineSegment(sketch, "E46.6.42.0", {"start": v(85.84, -28.68) * mm, "end": v(74.43, -24.97) * mm});
            skLineSegment(sketch, "E46.9.42.0", {"start": v(85.84, -28.68) * mm, "end": v(86.3, -27.25) * mm});
            skLineSegment(sketch, "E46.2.43.0", {"start": v(76.63, -17.05) * mm, "end": v(76.94, -15.59) * mm});
            skLineSegment(sketch, "E46.3.43.0", {"start": v(88.68, -18.08) * mm, "end": v(76.94, -15.59) * mm});
            skLineSegment(sketch, "E46.6.43.0", {"start": v(88.37, -19.55) * mm, "end": v(76.63, -17.05) * mm});
            skLineSegment(sketch, "E46.9.43.0", {"start": v(88.37, -19.55) * mm, "end": v(88.68, -18.08) * mm});
            skLineSegment(sketch, "E46.2.44.0", {"start": v(78, -8.95) * mm, "end": v(78.15, -7.46) * mm});
            skLineSegment(sketch, "E46.3.44.0", {"start": v(90.08, -8.71) * mm, "end": v(78.15, -7.46) * mm});
            skLineSegment(sketch, "E46.6.44.0", {"start": v(89.93, -10.2) * mm, "end": v(78, -8.95) * mm});
            skLineSegment(sketch, "E46.9.44.0", {"start": v(89.93, -10.2) * mm, "end": v(90.08, -8.71) * mm});
            skLineSegment(sketch, "E46.2.45.0", {"start": v(78.5, -0.75) * mm, "end": v(78.5, 0.75) * mm});
            skLineSegment(sketch, "E46.3.45.0", {"start": v(90.5, 0.75) * mm, "end": v(78.5, 0.75) * mm});
            skLineSegment(sketch, "E46.6.45.0", {"start": v(90.5, -0.75) * mm, "end": v(78.5, -0.75) * mm});
            skLineSegment(sketch, "E46.9.45.0", {"start": v(90.5, -0.75) * mm, "end": v(90.5, 0.75) * mm});
            skLineSegment(sketch, "E46.2.46.0", {"start": v(78.15, 7.46) * mm, "end": v(78, 8.95) * mm});
            skLineSegment(sketch, "E46.3.46.0", {"start": v(89.93, 10.2) * mm, "end": v(78, 8.95) * mm});
            skLineSegment(sketch, "E46.6.46.0", {"start": v(90.08, 8.71) * mm, "end": v(78.15, 7.46) * mm});
            skLineSegment(sketch, "E46.9.46.0", {"start": v(90.08, 8.71) * mm, "end": v(89.93, 10.2) * mm});
            skLineSegment(sketch, "E46.2.47.0", {"start": v(76.94, 15.59) * mm, "end": v(76.63, 17.05) * mm});
            skLineSegment(sketch, "E46.3.47.0", {"start": v(88.37, 19.55) * mm, "end": v(76.63, 17.05) * mm});
            skLineSegment(sketch, "E46.6.47.0", {"start": v(88.68, 18.08) * mm, "end": v(76.94, 15.59) * mm});
            skLineSegment(sketch, "E46.9.47.0", {"start": v(88.68, 18.08) * mm, "end": v(88.37, 19.55) * mm});
            skLineSegment(sketch, "E46.2.48.0", {"start": v(74.89, 23.54) * mm, "end": v(74.43, 24.97) * mm});
            skLineSegment(sketch, "E46.3.48.0", {"start": v(85.84, 28.68) * mm, "end": v(74.43, 24.97) * mm});
            skLineSegment(sketch, "E46.6.48.0", {"start": v(86.3, 27.25) * mm, "end": v(74.89, 23.54) * mm});
            skLineSegment(sketch, "E46.9.48.0", {"start": v(86.3, 27.25) * mm, "end": v(85.84, 28.68) * mm});
            skLineSegment(sketch, "E46.2.49.0", {"start": v(72.02, 31.24) * mm, "end": v(71.4, 32.61) * mm});
            skLineSegment(sketch, "E46.3.49.0", {"start": v(82.37, 37.5) * mm, "end": v(71.4, 32.61) * mm});
            skLineSegment(sketch, "E46.6.49.0", {"start": v(82.98, 36.12) * mm, "end": v(72.02, 31.24) * mm});
            skLineSegment(sketch, "E46.9.49.0", {"start": v(82.98, 36.12) * mm, "end": v(82.37, 37.5) * mm});
            skLineSegment(sketch, "E46.2.50.0", {"start": v(68.36, 38.6) * mm, "end": v(67.6, 39.9) * mm});
            skLineSegment(sketch, "E46.3.50.0", {"start": v(78, 45.9) * mm, "end": v(67.6, 39.9) * mm});
            skLineSegment(sketch, "E46.6.50.0", {"start": v(78.75, 44.6) * mm, "end": v(68.36, 38.6) * mm});
            skLineSegment(sketch, "E46.9.50.0", {"start": v(78.75, 44.6) * mm, "end": v(78, 45.9) * mm});
            skLineSegment(sketch, "E46.2.51.0", {"start": v(63.95, 45.53) * mm, "end": v(63.07, 46.75) * mm});
            skLineSegment(sketch, "E46.3.51.0", {"start": v(72.78, 53.8) * mm, "end": v(63.07, 46.75) * mm});
            skLineSegment(sketch, "E46.6.51.0", {"start": v(73.66, 52.59) * mm, "end": v(63.95, 45.53) * mm});
            skLineSegment(sketch, "E46.9.51.0", {"start": v(73.66, 52.59) * mm, "end": v(72.78, 53.8) * mm});
            skLineSegment(sketch, "E46.2.52.0", {"start": v(58.84, 51.97) * mm, "end": v(57.84, 53.08) * mm});
            skLineSegment(sketch, "E46.3.52.0", {"start": v(66.75, 61.11) * mm, "end": v(57.84, 53.08) * mm});
            skLineSegment(sketch, "E46.6.52.0", {"start": v(67.76, 60) * mm, "end": v(58.84, 51.97) * mm});
            skLineSegment(sketch, "E46.9.52.0", {"start": v(67.76, 60) * mm, "end": v(66.75, 61.11) * mm});
            skLineSegment(sketch, "E46.2.53.0", {"start": v(53.08, 57.84) * mm, "end": v(51.97, 58.84) * mm});
            skLineSegment(sketch, "E46.3.53.0", {"start": v(60, 67.76) * mm, "end": v(51.97, 58.84) * mm});
            skLineSegment(sketch, "E46.6.53.0", {"start": v(61.11, 66.75) * mm, "end": v(53.08, 57.84) * mm});
            skLineSegment(sketch, "E46.9.53.0", {"start": v(61.11, 66.75) * mm, "end": v(60, 67.76) * mm});
            skLineSegment(sketch, "E46.2.54.0", {"start": v(46.75, 63.07) * mm, "end": v(45.53, 63.95) * mm});
            skLineSegment(sketch, "E46.3.54.0", {"start": v(52.59, 73.66) * mm, "end": v(45.53, 63.95) * mm});
            skLineSegment(sketch, "E46.6.54.0", {"start": v(53.8, 72.78) * mm, "end": v(46.75, 63.07) * mm});
            skLineSegment(sketch, "E46.9.54.0", {"start": v(53.8, 72.78) * mm, "end": v(52.59, 73.66) * mm});
            skLineSegment(sketch, "E46.2.55.0", {"start": v(39.9, 67.6) * mm, "end": v(38.6, 68.36) * mm});
            skLineSegment(sketch, "E46.3.55.0", {"start": v(44.6, 78.75) * mm, "end": v(38.6, 68.36) * mm});
            skLineSegment(sketch, "E46.6.55.0", {"start": v(45.9, 78) * mm, "end": v(39.9, 67.6) * mm});
            skLineSegment(sketch, "E46.9.55.0", {"start": v(45.9, 78) * mm, "end": v(44.6, 78.75) * mm});
            skLineSegment(sketch, "E46.2.56.0", {"start": v(32.61, 71.4) * mm, "end": v(31.24, 72.02) * mm});
            skLineSegment(sketch, "E46.3.56.0", {"start": v(36.12, 82.98) * mm, "end": v(31.24, 72.02) * mm});
            skLineSegment(sketch, "E46.6.56.0", {"start": v(37.5, 82.37) * mm, "end": v(32.61, 71.4) * mm});
            skLineSegment(sketch, "E46.9.56.0", {"start": v(37.5, 82.37) * mm, "end": v(36.12, 82.98) * mm});
            skLineSegment(sketch, "E46.2.57.0", {"start": v(24.97, 74.43) * mm, "end": v(23.54, 74.89) * mm});
            skLineSegment(sketch, "E46.3.57.0", {"start": v(27.25, 86.3) * mm, "end": v(23.54, 74.89) * mm});
            skLineSegment(sketch, "E46.6.57.0", {"start": v(28.68, 85.84) * mm, "end": v(24.97, 74.43) * mm});
            skLineSegment(sketch, "E46.9.57.0", {"start": v(28.68, 85.84) * mm, "end": v(27.25, 86.3) * mm});
            skLineSegment(sketch, "E46.2.58.0", {"start": v(17.05, 76.63) * mm, "end": v(15.59, 76.94) * mm});
            skLineSegment(sketch, "E46.3.58.0", {"start": v(18.08, 88.68) * mm, "end": v(15.59, 76.94) * mm});
            skLineSegment(sketch, "E46.6.58.0", {"start": v(19.55, 88.37) * mm, "end": v(17.05, 76.63) * mm});
            skLineSegment(sketch, "E46.9.58.0", {"start": v(19.55, 88.37) * mm, "end": v(18.08, 88.68) * mm});
            skLineSegment(sketch, "E46.2.59.0", {"start": v(8.95, 78) * mm, "end": v(7.46, 78.15) * mm});
            skLineSegment(sketch, "E46.3.59.0", {"start": v(8.71, 90.08) * mm, "end": v(7.46, 78.15) * mm});
            skLineSegment(sketch, "E46.6.59.0", {"start": v(10.2, 89.93) * mm, "end": v(8.95, 78) * mm});
            skLineSegment(sketch, "E46.9.59.0", {"start": v(10.2, 89.93) * mm, "end": v(8.71, 90.08) * mm});
            skSolve(sketch);
        }
        {
            var Q0;
            Q0 = qSketchRegion(id + "F27", true);
            extrude(context, id + "F28", {"entities" : qUnion([Q0]), "operationType" : NewBodyOperationType.REMOVE, "oppositeDirection" : true, "depth" : 0.2 * mm, "offsetDistance" : 25 * mm});
        }
        {
            var Q0;
            Q0=makeQuery(id+"F26.boolean.opBoolean","COPY",FACE,{"derivedFrom":makeQuery(id+"F26.opExtrude","CAP_FACE",FACE,{"disambiguationData":[OSD([sQuery(id+"F25.wireOp",EDGE,"E41.bottom"),sQuery(id+"F25.wireOp",EDGE,"E41.top"),sQuery(id+"F25.wireOp",EDGE,"E41.left"),sQuery(id+"F25.wireOp",EDGE,"E41.right")])],"isStart":false})});
            extrude(context, id + "F29", {"entities" : qUnion([Q0]), "depth" : 1 * mm, "offsetDistance" : 25 * mm});
        }
        {
            var Q0;
            Q0=makeQuery(id+"F28.boolean.opBoolean","COPY",FACE,{"derivedFrom":makeQuery(id+"F28.opExtrude","CAP_FACE",FACE,{"disambiguationData":[OSD([sQuery(id+"F27.wireOp",EDGE,"E46.2.59.0"),sQuery(id+"F27.wireOp",EDGE,"E46.3.59.0"),sQuery(id+"F27.wireOp",EDGE,"E46.6.59.0"),sQuery(id+"F27.wireOp",EDGE,"E46.9.59.0")])],"isStart":false})});
            extrude(context, id + "F30", {"entities" : qUnion([Q0]), "depth" : 0.4 * mm, "offsetDistance" : 25 * mm});
        }
        {
            var Q0;
            Q0=makeQuery(id+"F15.opExtrude","CAP_FACE",FACE,{"disambiguationData":[OSD([sQuery(id+"F14.wireOp",EDGE,"E21.0"),sQuery(id+"F14.wireOp",EDGE,"E22"),sQuery(id+"F14.wireOp",EDGE,"E23"),sQuery(id+"F14.wireOp",EDGE,"E24"),sQuery(id+"F14.wireOp",EDGE,"E25.MirrorCS"),sQuery(id+"F14.wireOp",EDGE,"E26.MirrorCS"),sQuery(id+"F14.wireOp",EDGE,"E27.1.0"),sQuery(id+"F14.wireOp",EDGE,"E27.1.1"),sQuery(id+"F14.wireOp",EDGE,"E27.1.2"),sQuery(id+"F14.wireOp",EDGE,"E27.1.3"),sQuery(id+"F14.wireOp",EDGE,"E27.2.0"),sQuery(id+"F14.wireOp",EDGE,"E27.2.1"),sQuery(id+"F14.wireOp",EDGE,"E27.2.2"),sQuery(id+"F14.wireOp",EDGE,"E27.2.3"),sQuery(id+"F14.wireOp",EDGE,"E28.1.3.0"),sQuery(id+"F14.wireOp",EDGE,"E28.3.3.0"),sQuery(id+"F14.wireOp",EDGE,"E28.6.3.0"),sQuery(id+"F14.wireOp",EDGE,"E28.9.3.0"),sQuery(id+"F14.wireOp",EDGE,"E28.1.4.0"),sQuery(id+"F14.wireOp",EDGE,"E28.3.4.0"),sQuery(id+"F14.wireOp",EDGE,"E28.6.4.0"),sQuery(id+"F14.wireOp",EDGE,"E28.9.4.0"),sQuery(id+"F14.wireOp",EDGE,"E28.1.5.0"),sQuery(id+"F14.wireOp",EDGE,"E28.3.5.0"),sQuery(id+"F14.wireOp",EDGE,"E28.6.5.0"),sQuery(id+"F14.wireOp",EDGE,"E28.9.5.0"),sQuery(id+"F14.wireOp",EDGE,"E28.1.6.0"),sQuery(id+"F14.wireOp",EDGE,"E28.3.6.0"),sQuery(id+"F14.wireOp",EDGE,"E28.6.6.0"),sQuery(id+"F14.wireOp",EDGE,"E28.9.6.0"),sQuery(id+"F14.wireOp",EDGE,"E28.1.7.0"),sQuery(id+"F14.wireOp",EDGE,"E28.3.7.0"),sQuery(id+"F14.wireOp",EDGE,"E28.6.7.0"),sQuery(id+"F14.wireOp",EDGE,"E28.9.7.0"),sQuery(id+"F14.wireOp",EDGE,"E28.1.8.0"),sQuery(id+"F14.wireOp",EDGE,"E28.3.8.0"),sQuery(id+"F14.wireOp",EDGE,"E28.6.8.0"),sQuery(id+"F14.wireOp",EDGE,"E28.9.8.0"),sQuery(id+"F14.wireOp",EDGE,"E28.1.9.0"),sQuery(id+"F14.wireOp",EDGE,"E28.3.9.0"),sQuery(id+"F14.wireOp",EDGE,"E28.6.9.0"),sQuery(id+"F14.wireOp",EDGE,"E28.9.9.0"),sQuery(id+"F14.wireOp",EDGE,"E28.1.10.0"),sQuery(id+"F14.wireOp",EDGE,"E28.3.10.0"),sQuery(id+"F14.wireOp",EDGE,"E28.6.10.0"),sQuery(id+"F14.wireOp",EDGE,"E28.9.10.0"),sQuery(id+"F14.wireOp",EDGE,"E28.1.11.0"),sQuery(id+"F14.wireOp",EDGE,"E28.3.11.0"),sQuery(id+"F14.wireOp",EDGE,"E28.6.11.0"),sQuery(id+"F14.wireOp",EDGE,"E28.9.11.0"),sQuery(id+"F14.wireOp",EDGE,"E28.1.12.0"),sQuery(id+"F14.wireOp",EDGE,"E28.3.12.0"),sQuery(id+"F14.wireOp",EDGE,"E28.6.12.0"),sQuery(id+"F14.wireOp",EDGE,"E28.9.12.0"),sQuery(id+"F14.wireOp",EDGE,"E28.1.13.0"),sQuery(id+"F14.wireOp",EDGE,"E28.3.13.0"),sQuery(id+"F14.wireOp",EDGE,"E28.6.13.0"),sQuery(id+"F14.wireOp",EDGE,"E28.9.13.0"),sQuery(id+"F14.wireOp",EDGE,"E28.1.14.0"),sQuery(id+"F14.wireOp",EDGE,"E28.3.14.0"),sQuery(id+"F14.wireOp",EDGE,"E28.6.14.0"),sQuery(id+"F14.wireOp",EDGE,"E28.9.14.0"),sQuery(id+"F14.wireOp",EDGE,"E28.1.15.0"),sQuery(id+"F14.wireOp",EDGE,"E28.3.15.0"),sQuery(id+"F14.wireOp",EDGE,"E28.6.15.0"),sQuery(id+"F14.wireOp",EDGE,"E28.9.15.0"),sQuery(id+"F14.wireOp",EDGE,"E28.1.16.0"),sQuery(id+"F14.wireOp",EDGE,"E28.3.16.0"),sQuery(id+"F14.wireOp",EDGE,"E28.6.16.0"),sQuery(id+"F14.wireOp",EDGE,"E28.9.16.0"),sQuery(id+"F14.wireOp",EDGE,"E28.1.17.0"),sQuery(id+"F14.wireOp",EDGE,"E28.3.17.0"),sQuery(id+"F14.wireOp",EDGE,"E28.6.17.0"),sQuery(id+"F14.wireOp",EDGE,"E28.9.17.0"),sQuery(id+"F14.wireOp",EDGE,"E28.1.18.0"),sQuery(id+"F14.wireOp",EDGE,"E28.3.18.0"),sQuery(id+"F14.wireOp",EDGE,"E28.6.18.0"),sQuery(id+"F14.wireOp",EDGE,"E28.9.18.0"),sQuery(id+"F14.wireOp",EDGE,"E28.1.19.0"),sQuery(id+"F14.wireOp",EDGE,"E28.3.19.0"),sQuery(id+"F14.wireOp",EDGE,"E28.6.19.0"),sQuery(id+"F14.wireOp",EDGE,"E28.9.19.0"),sQuery(id+"F14.wireOp",EDGE,"E28.1.20.0"),sQuery(id+"F14.wireOp",EDGE,"E28.3.20.0"),sQuery(id+"F14.wireOp",EDGE,"E28.6.20.0"),sQuery(id+"F14.wireOp",EDGE,"E28.9.20.0"),sQuery(id+"F14.wireOp",EDGE,"E28.1.21.0"),sQuery(id+"F14.wireOp",EDGE,"E28.3.21.0"),sQuery(id+"F14.wireOp",EDGE,"E28.6.21.0"),sQuery(id+"F14.wireOp",EDGE,"E28.9.21.0"),sQuery(id+"F14.wireOp",EDGE,"E28.1.22.0"),sQuery(id+"F14.wireOp",EDGE,"E28.3.22.0"),sQuery(id+"F14.wireOp",EDGE,"E28.6.22.0"),sQuery(id+"F14.wireOp",EDGE,"E28.9.22.0"),sQuery(id+"F14.wireOp",EDGE,"E28.1.23.0"),sQuery(id+"F14.wireOp",EDGE,"E28.3.23.0"),sQuery(id+"F14.wireOp",EDGE,"E28.6.23.0"),sQuery(id+"F14.wireOp",EDGE,"E28.9.23.0"),sQuery(id+"F14.wireOp",EDGE,"E28.1.24.0"),sQuery(id+"F14.wireOp",EDGE,"E28.3.24.0"),sQuery(id+"F14.wireOp",EDGE,"E28.6.24.0"),sQuery(id+"F14.wireOp",EDGE,"E28.9.24.0"),sQuery(id+"F14.wireOp",EDGE,"E28.1.25.0"),sQuery(id+"F14.wireOp",EDGE,"E28.3.25.0"),sQuery(id+"F14.wireOp",EDGE,"E28.6.25.0"),sQuery(id+"F14.wireOp",EDGE,"E28.9.25.0"),sQuery(id+"F14.wireOp",EDGE,"E28.1.26.0"),sQuery(id+"F14.wireOp",EDGE,"E28.3.26.0"),sQuery(id+"F14.wireOp",EDGE,"E28.6.26.0"),sQuery(id+"F14.wireOp",EDGE,"E28.9.26.0"),sQuery(id+"F14.wireOp",EDGE,"E28.1.27.0"),sQuery(id+"F14.wireOp",EDGE,"E28.3.27.0"),sQuery(id+"F14.wireOp",EDGE,"E28.6.27.0"),sQuery(id+"F14.wireOp",EDGE,"E28.9.27.0"),sQuery(id+"F14.wireOp",EDGE,"E28.1.28.0"),sQuery(id+"F14.wireOp",EDGE,"E28.3.28.0"),sQuery(id+"F14.wireOp",EDGE,"E28.6.28.0"),sQuery(id+"F14.wireOp",EDGE,"E28.9.28.0"),sQuery(id+"F14.wireOp",EDGE,"E28.1.29.0"),sQuery(id+"F14.wireOp",EDGE,"E28.3.29.0"),sQuery(id+"F14.wireOp",EDGE,"E28.6.29.0"),sQuery(id+"F14.wireOp",EDGE,"E28.9.29.0"),sQuery(id+"F14.wireOp",EDGE,"E28.1.30.0"),sQuery(id+"F14.wireOp",EDGE,"E28.3.30.0"),sQuery(id+"F14.wireOp",EDGE,"E28.6.30.0"),sQuery(id+"F14.wireOp",EDGE,"E28.9.30.0"),sQuery(id+"F14.wireOp",EDGE,"E28.1.31.0"),sQuery(id+"F14.wireOp",EDGE,"E28.3.31.0"),sQuery(id+"F14.wireOp",EDGE,"E28.6.31.0"),sQuery(id+"F14.wireOp",EDGE,"E28.9.31.0"),sQuery(id+"F14.wireOp",EDGE,"E28.1.32.0"),sQuery(id+"F14.wireOp",EDGE,"E28.3.32.0"),sQuery(id+"F14.wireOp",EDGE,"E28.6.32.0"),sQuery(id+"F14.wireOp",EDGE,"E28.9.32.0"),sQuery(id+"F14.wireOp",EDGE,"E28.1.33.0"),sQuery(id+"F14.wireOp",EDGE,"E28.3.33.0"),sQuery(id+"F14.wireOp",EDGE,"E28.6.33.0"),sQuery(id+"F14.wireOp",EDGE,"E28.9.33.0"),sQuery(id+"F14.wireOp",EDGE,"E28.1.34.0"),sQuery(id+"F14.wireOp",EDGE,"E28.3.34.0"),sQuery(id+"F14.wireOp",EDGE,"E28.6.34.0"),sQuery(id+"F14.wireOp",EDGE,"E28.9.34.0"),sQuery(id+"F14.wireOp",EDGE,"E28.1.35.0"),sQuery(id+"F14.wireOp",EDGE,"E28.3.35.0"),sQuery(id+"F14.wireOp",EDGE,"E28.6.35.0"),sQuery(id+"F14.wireOp",EDGE,"E28.9.35.0"),sQuery(id+"F14.wireOp",EDGE,"E28.1.36.0"),sQuery(id+"F14.wireOp",EDGE,"E28.3.36.0"),sQuery(id+"F14.wireOp",EDGE,"E28.6.36.0"),sQuery(id+"F14.wireOp",EDGE,"E28.9.36.0"),sQuery(id+"F14.wireOp",EDGE,"E28.1.37.0"),sQuery(id+"F14.wireOp",EDGE,"E28.3.37.0"),sQuery(id+"F14.wireOp",EDGE,"E28.6.37.0"),sQuery(id+"F14.wireOp",EDGE,"E28.9.37.0"),sQuery(id+"F14.wireOp",EDGE,"E28.1.38.0"),sQuery(id+"F14.wireOp",EDGE,"E28.3.38.0"),sQuery(id+"F14.wireOp",EDGE,"E28.6.38.0"),sQuery(id+"F14.wireOp",EDGE,"E28.9.38.0"),sQuery(id+"F14.wireOp",EDGE,"E28.1.39.0"),sQuery(id+"F14.wireOp",EDGE,"E28.3.39.0"),sQuery(id+"F14.wireOp",EDGE,"E28.6.39.0"),sQuery(id+"F14.wireOp",EDGE,"E28.9.39.0")])],"isStart":false});
            var sketch = newSketch(context, id + "F31", { "sketchPlane" : qUnion([Q0])});
            skCircle(sketch, "E47.0", {"center": v(0, 0) * mm, "radius": 3 * mm});
            skCircle(sketch, "E48.0", {"center": v(0, 0) * mm, "radius": 5 * mm});
            skSolve(sketch);
        }
        {
            var Q0;
            Q0 = qSketchRegion(id + "F31", true);
            extrude(context, id + "F32", {"entities" : qUnion([Q0]), "operationType" : NewBodyOperationType.ADD, "depth" : 5 * mm, "offsetDistance" : 25 * mm});
        }
        {
            var Q0;
            Q0=makeQuery(id+"F32.opExtrude","CAP_FACE",FACE,{"disambiguationData":[OSD([sQuery(id+"F31.wireOp",EDGE,"E47.0"),sQuery(id+"F31.wireOp",EDGE,"E48.0")])],"isStart":false});
            var sketch = newSketch(context, id + "F33", { "sketchPlane" : qUnion([Q0])});
            skCircle(sketch, "E49.0", {"center": v(0, 0) * mm, "radius": 3 * mm});
            skCircle(sketch, "E50.0", {"center": v(0, 0) * mm, "radius": 5 * mm});
            skLineSegment(sketch, "E51", {"start": v(0, 54) * mm, "end": v(1.5, 54) * mm});
            skLineSegment(sketch, "E52", {"start": v(1.5, 54) * mm, "end": v(3, 4) * mm});
            skLineSegment(sketch, "E53.MirrorCS", {"start": v(0, 54) * mm, "end": v(-1.5, 54) * mm});
            skLineSegment(sketch, "E54.MirrorCS", {"start": v(-1.5, 54) * mm, "end": v(-3, 4) * mm});
            skSolve(sketch);
        }
        {
            var Q0;
            Q0 = qSketchRegion(id + "F33", true);
            extrude(context, id + "F34", {"entities" : qUnion([Q0]), "operationType" : NewBodyOperationType.ADD, "depth" : 1 * mm, "offsetDistance" : 25 * mm});
        }
        {
            var Q0;
            Q0=makeQuery(id+"F6.opExtrude","CAP_FACE",FACE,{"disambiguationData":[OSD([sQuery(id+"F0.wireOp",EDGE,"E0")])],"isStart":false});
            var sketch = newSketch(context, id + "F35", { "sketchPlane" : qUnion([Q0])});
            skCircle(sketch, "E55", {"center": v(0, 0) * mm, "radius": 5 * mm});
            skLineSegment(sketch, "E56", {"start": v(0, 84.58) * mm, "end": v(0.5, 84.58) * mm});
            skLineSegment(sketch, "E57", {"start": v(0.5, 84.58) * mm, "end": v(2, 4.58) * mm});
            skLineSegment(sketch, "E58.MirrorCS", {"start": v(0, 84.58) * mm, "end": v(-0.5, 84.58) * mm});
            skLineSegment(sketch, "E59.MirrorCS", {"start": v(-0.5, 84.58) * mm, "end": v(-2, 4.58) * mm});
            skSolve(sketch);
        }
        {
            var Q0;
            Q0 = qSketchRegion(id + "F35", true);
            extrude(context, id + "F36", {"entities" : qUnion([Q0]), "operationType" : NewBodyOperationType.ADD, "oppositeDirection" : true, "depth" : 1 * mm, "offsetDistance" : 25 * mm});
        }
    });
